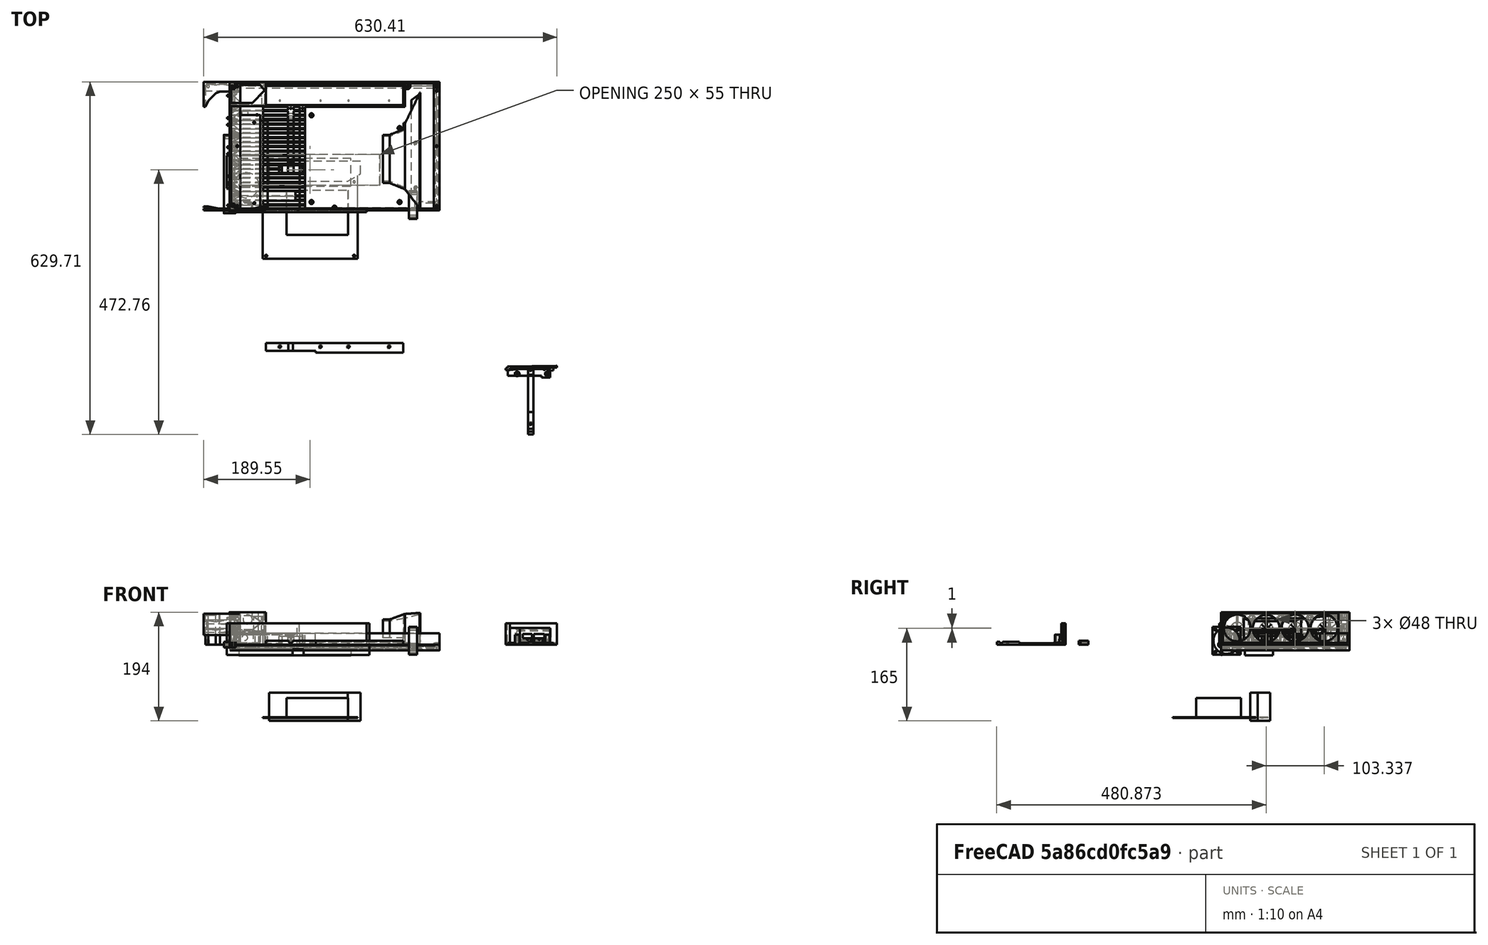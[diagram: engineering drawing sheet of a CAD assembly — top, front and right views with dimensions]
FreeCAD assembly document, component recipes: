
FREECAD ASSEMBLY — COMPONENT RECIPES ("4_fan_duct_version")

This assembly document has 13 components, labeled P0..P12 below (a component is one placed body or linked part). 13 of them carry a construction recipe — the FreeCAD feature program that regenerates the part from scratch, quoted from this document or its linked companion documents; the rest are supplied as boundary geometry only. No exploded tour is included for this assembly.
NOTE — document 2 of 2 of this assembly tour. The two overview renders and the header above are repeated from document 1; the component sections below continue where the previous document stopped.
COMPONENT P2 — recipe-attached ("FAN_SHROUD001", modeled in this document).
Construction recipe (the document's own serialized feature program — sketch geometry with constraints, then the solid features built on it; lengths are millimeters unless a unit is written):

FEATURE [Sketcher::SketchObject] Sketch057
  ArcFitTolerance = 1e-06
  AttachmentSupport = -> [XY_Plane031]
  FullyConstrained = false
  MakeInternals = false
  MapMode = 5
  expr: Constraints[10] = <<components>>.frame_h
  expr: Constraints[21] = <<choices>>.mb_front_edge_gap
  expr: Constraints[25] = 10.16 + 22.86
  expr: Constraints[27] = <<components>>.fan_w + <<choices>>.exit_w + <<choices>>.shroud_mb_space
  expr: Constraints[37] = <<components>>.fan_w
  expr: Constraints[38] = <<components>>.fan_h * 4 + 3 * <<choices>>.fan_gap
  expr: Constraints[40] = <<choices>>.exit_w
  expr: Constraints[71] = <<components>>.fan_h + <<choices>>.fan_gap
  expr: Constraints[9] = <<components>>.frame_w
  sketch-geometry (28):
    g0: LineSegment [constr] StartX=0 StartY=0 StartZ=0 EndX=375 EndY=0 EndZ=0
    g1: LineSegment [constr] StartX=375 StartY=0 StartZ=0 EndX=375 EndY=229.5 EndZ=0
    g2: LineSegment [constr] StartX=375 StartY=229.5 StartZ=0 EndX=0 EndY=229.5 EndZ=0
    g3: LineSegment [constr] StartX=0 StartY=229.5 StartZ=0 EndX=0 EndY=0 EndZ=0
    g4: LineSegment [constr] StartX=140 StartY=180 StartZ=0 EndX=140 EndY=10 EndZ=0
    g5: LineSegment [constr] StartX=140 StartY=10 StartZ=0 EndX=310 EndY=10 EndZ=0
    g6: LineSegment [constr] StartX=310 StartY=10 StartZ=0 EndX=310 EndY=180 EndZ=0
    g7: LineSegment [constr] StartX=310 StartY=180 StartZ=0 EndX=140 EndY=180 EndZ=0
    g8: LineSegment [constr] StartX=303.65 StartY=146.98 StartZ=0 EndX=303.65 EndY=10 EndZ=0
    g9: Circle CenterX=303.65 CenterY=146.98 CenterZ=0 NormalX=0 NormalY=0 NormalZ=1 AngleXU=0 Radius=1.75
    g10: LineSegment [constr] StartX=339 StartY=4 StartZ=0 EndX=356 EndY=4 EndZ=0
    g11: LineSegment [constr] StartX=356 StartY=4 StartZ=0 EndX=356 EndY=210 EndZ=0
    g12: LineSegment [constr] StartX=356 StartY=210 StartZ=0 EndX=339 EndY=210 EndZ=0
    g13: LineSegment [constr] StartX=339 StartY=210 StartZ=0 EndX=339 EndY=4 EndZ=0
    g14: LineSegment [constr] StartX=183 StartY=132 StartZ=0 EndX=183 EndY=52 EndZ=0
    g15: LineSegment [constr] StartX=183 StartY=52 StartZ=0 EndX=293 EndY=52 EndZ=0
    g16: LineSegment [constr] StartX=293 StartY=52 StartZ=0 EndX=293 EndY=132 EndZ=0
    g17: LineSegment [constr] StartX=293 StartY=132 StartZ=0 EndX=183 EndY=132 EndZ=0
    g18: LineSegment StartX=273.053 StartY=132 StartZ=0 EndX=286 EndY=132 EndZ=0
    g19: LineSegment StartX=286 StartY=132 StartZ=0 EndX=309.823 EndY=145.872 EndZ=0
    g20: LineSegment StartX=309.823 StartY=145.872 StartZ=0 EndX=339 EndY=158 EndZ=0
    g21: LineSegment StartX=339 StartY=158 StartZ=0 EndX=356 EndY=158 EndZ=0
    g22: LineSegment StartX=356 StartY=158 StartZ=0 EndX=356 EndY=4 EndZ=0
    g23: LineSegment StartX=356 StartY=4 StartZ=0 EndX=339 EndY=4 EndZ=0
    g24: LineSegment StartX=339 StartY=4 StartZ=0 EndX=309.823 EndY=36.5092 EndZ=0
    g25: LineSegment StartX=309.823 StartY=36.5092 StartZ=0 EndX=286 EndY=52 EndZ=0
    g26: LineSegment StartX=286 StartY=52 StartZ=0 EndX=273.053 EndY=52 EndZ=0
    g27: LineSegment StartX=273.053 StartY=52 StartZ=0 EndX=273.053 EndY=132 EndZ=0
  constraints (76):
    c: Coincident(g0,g1)
    c: Coincident(g1,g2)
    c: Coincident(g2,g3)
    c: Coincident(g3,g0)
    c: Horizontal(g0)
    c: Horizontal(g2)
    c: Vertical(g1)
    c: Vertical(g3)
    c: Coincident(g0,g-1)
    c: DistanceX(g2,g2) = 375
    c: DistanceY(g1,g1) = 229.5
    c: Coincident(g4,g5)
    c: Coincident(g5,g6)
    c: Coincident(g6,g7)
    c: Coincident(g7,g4)
    c: Vertical(g4)
    c: Vertical(g6)
    c: Horizontal(g5)
    c: Horizontal(g7)
    c: Distance(g4,g6) = 170
    c: Distance(g5,g7) = 170
    c: DistanceY(g5) = 10
    c: Vertical(g8)
    c: PointOnObject(g8,g5)
    c: Distance(g8,g6) = 6.35
    c: Distance(g8,g7) = 33.02
    c: Diameter(g9) = 3.5
    c: Distance(g5,g1) = 65
    c: Coincident(g9,g8)
    c: Coincident(g10,g11)
    c: Coincident(g11,g12)
    c: Coincident(g12,g13)
    c: Coincident(g13,g10)
    c: Horizontal(g10)
    c: Horizontal(g12)
    c: Vertical(g11)
    c: Vertical(g13)
    c: DistanceX(g12,g12) = 17
    c: DistanceY(g13,g13) = 206
    c: DistanceY(g10) = 4
    c: Distance(g10,g1) = 19
    c: Coincident(g14,g15)
    c: Coincident(g15,g16)
    c: Coincident(g16,g17)
    c: Coincident(g17,g14)
    c: Vertical(g14)
    c: Vertical(g16)
    c: Horizontal(g15)
    c: Horizontal(g17)
    c: Distance(g14,g16) = 110
    c: Distance(g15,g17) = 80
    c: Distance(g15,g6) = 17
    c: Distance(g15,g5) = 42
    c: Horizontal(g18)
    c: Coincident(g18,g19)
    c: Coincident(g19,g20)
    c: PointOnObject(g20,g13)
    c: Coincident(g20,g21)
    c: PointOnObject(g21,g11)
    c: Horizontal(g21)
    c: Coincident(g21,g22)
    c: Coincident(g22,g10)
    c: Coincident(g22,g23)
    c: Coincident(g23,g10)
    c: Coincident(g23,g24)
    c: Coincident(g24,g25)
    c: Coincident(g25,g26)
    c: Horizontal(g26)
    c: Coincident(g26,g27)
    c: Coincident(g27,g18)
    c: Vertical(g27)
    c: Distance(g20,g12) = 52
    c: PointOnObject(g25,g15)
    c: PointOnObject(g18,g17)
    c: Equal(g18,g26)
    c: Distance(g18,g6) = 24
FEATURE [PartDesign::Plane] DatumPlane010
  AttachmentOffset = pos=(0,0,340) rot=(0,0,1;0rad)
  AttachmentSupport = -> [YZ_Plane031]
  Length = 262.721
  MapMode = 5
  Placement = pos=(340,0,0) rot=(0.57735,0.57735,0.57735;2.0944rad)
  ResizeMode = 0
  Width = 109.471
  expr: .AttachmentOffset.Base.z = <<components>>.frame_w - <<choices>>.exit_w - <<components>>.fan_w + 1
FEATURE [PartDesign::Plane] DatumPlane011
  AttachmentOffset = pos=(0,0,313) rot=(0,0,1;0rad)
  AttachmentSupport = -> [YZ_Plane031]
  Length = 262.721
  MapMode = 5
  Placement = pos=(313,0,0) rot=(0.57735,0.57735,0.57735;2.0944rad)
  ResizeMode = 0
  Width = 109.471
  expr: .AttachmentOffset.Base.z = <<components>>.frame_w - <<choices>>.exit_w - <<components>>.fan_w - <<choices>>.shroud_mb_space + 3
FEATURE [PartDesign::Plane] DatumPlane012
  AttachmentOffset = pos=(0,0,286) rot=(0,0,1;0rad)
  AttachmentSupport = -> [YZ_Plane031]
  Length = 262.721
  MapMode = 5
  Placement = pos=(286,0,0) rot=(0.57735,0.57735,0.57735;2.0944rad)
  ResizeMode = 0
  Width = 109.471
  expr: .AttachmentOffset.Base.z = <<components>>.frame_w - <<choices>>.exit_w - <<components>>.fan_w - <<choices>>.shroud_mb_space - 24
FEATURE [PartDesign::Plane] DatumPlane013
  AttachmentOffset = pos=(0,0,276) rot=(0,0,1;0rad)
  AttachmentSupport = -> [YZ_Plane031]
  Length = 262.721
  MapMode = 5
  Placement = pos=(276,0,0) rot=(0.57735,0.57735,0.57735;2.0944rad)
  ResizeMode = 0
  Width = 109.471
  expr: .AttachmentOffset.Base.z = <<components>>.frame_w - <<choices>>.exit_w - <<components>>.fan_w - <<choices>>.shroud_mb_space - 24 - 10
FEATURE [Sketcher::SketchObject] Sketch058
  ArcFitTolerance = 1e-06
  AttachmentSupport = -> [DatumPlane012]
  FullyConstrained = true
  MakeInternals = false
  MapMode = 5
  Placement = pos=(286,0,0) rot=(0.57735,0.57735,0.57735;2.0944rad)
  expr: Constraints[16] = <<choices>>.shroud_wall_thickness
  sketch-geometry (8):
    g0: LineSegment StartX=49 StartY=12 StartZ=0 EndX=49 EndY=45 EndZ=0
    g1: LineSegment StartX=49 StartY=45 StartZ=0 EndX=135 EndY=45 EndZ=0
    g2: LineSegment StartX=135 StartY=45 StartZ=0 EndX=135 EndY=19 EndZ=0
    g3: LineSegment StartX=135 StartY=19 StartZ=0 EndX=132 EndY=19 EndZ=0
    g4: LineSegment StartX=132 StartY=19 StartZ=0 EndX=132 EndY=42 EndZ=0
    g5: LineSegment StartX=132 StartY=42 StartZ=0 EndX=52 EndY=42 EndZ=0
    g6: LineSegment StartX=52 StartY=42 StartZ=0 EndX=52 EndY=12 EndZ=0
    g7: LineSegment StartX=52 StartY=12 StartZ=0 EndX=49 EndY=12 EndZ=0
  constraints (24):
    c: Vertical(g0)
    c: Coincident(g0,g1)
    c: Horizontal(g1)
    c: Coincident(g1,g2)
    c: Vertical(g2)
    c: Coincident(g2,g3)
    c: Horizontal(g3)
    c: Coincident(g3,g4)
    c: Vertical(g4)
    c: Coincident(g4,g5)
    c: Horizontal(g5)
    c: Coincident(g5,g6)
    c: Vertical(g6)
    c: Coincident(g6,g7)
    c: Coincident(g7,g0)
    c: Horizontal(g7)
    c: DistanceX(g3,g3) = 3
    c: Equal(g7,g3)
    c: DistanceY(g5) = 42
    c: DistanceY(g6,g6) = 30
    c: DistanceY(g4,g4) = 23
    c: DistanceX(g5) = 52
    c: DistanceX(g5,g5) = 80
    c: Distance(g5,g1) = 3
FEATURE [Sketcher::SketchObject] Sketch059
  ArcFitTolerance = 1e-06
  AttachmentSupport = -> [DatumPlane012]
  FullyConstrained = true
  MakeInternals = false
  MapMode = 5
  Placement = pos=(286,0,0) rot=(0.57735,0.57735,0.57735;2.0944rad)
  expr: Constraints[16] = <<choices>>.shroud_wall_thickness
  sketch-geometry (8):
    g0: LineSegment StartX=49 StartY=12 StartZ=0 EndX=49 EndY=45 EndZ=0
    g1: LineSegment StartX=49 StartY=45 StartZ=0 EndX=135 EndY=45 EndZ=0
    g2: LineSegment StartX=135 StartY=45 StartZ=0 EndX=135 EndY=19 EndZ=0
    g3: LineSegment StartX=135 StartY=19 StartZ=0 EndX=132 EndY=19 EndZ=0
    g4: LineSegment StartX=132 StartY=19 StartZ=0 EndX=132 EndY=42 EndZ=0
    g5: LineSegment StartX=132 StartY=42 StartZ=0 EndX=52 EndY=42 EndZ=0
    g6: LineSegment StartX=52 StartY=42 StartZ=0 EndX=52 EndY=12 EndZ=0
    g7: LineSegment StartX=52 StartY=12 StartZ=0 EndX=49 EndY=12 EndZ=0
  constraints (24):
    c: Vertical(g0)
    c: Coincident(g0,g1)
    c: Horizontal(g1)
    c: Coincident(g1,g2)
    c: Vertical(g2)
    c: Coincident(g2,g3)
    c: Horizontal(g3)
    c: Coincident(g3,g4)
    c: Vertical(g4)
    c: Coincident(g4,g5)
    c: Horizontal(g5)
    c: Coincident(g5,g6)
    c: Vertical(g6)
    c: Coincident(g6,g7)
    c: Coincident(g7,g0)
    c: Horizontal(g7)
    c: DistanceX(g3,g3) = 3
    c: Equal(g7,g3)
    c: DistanceY(g5) = 42
    c: DistanceY(g6,g6) = 30
    c: DistanceY(g4,g4) = 23
    c: DistanceX(g5) = 52
    c: DistanceX(g5,g5) = 80
    c: Distance(g0,g5) = 3
FEATURE [PartDesign::Pad] Pad027
  Direction = (1,0,0)
  Length = 12
  Length2 = 10
  Placement = pos=(286,0,0) rot=(0.57735,0.57735,0.57735;2.0944rad)
  Profile = -> Sketch058
  ReferenceAxis = -> Sketch058 [N_Axis]
  Refine = true
  Reversed = true
  Suppressed = false
  Type = 0
FEATURE [Sketcher::SketchObject] Sketch060
  ArcFitTolerance = 1e-06
  AttachmentSupport = -> [DatumPlane011]
  FullyConstrained = false
  MakeInternals = false
  MapMode = 5
  Placement = pos=(313,0,0) rot=(0.57735,0.57735,0.57735;2.0944rad)
  expr: Constraints[17] = <<choices>>.shroud_wall_thickness
  expr: Constraints[25] = <<choices>>.exit_height + 3 - <<choices>>.base_under_mb_thickness - 2
  sketch-geometry (9):
    g0: LineSegment StartX=41 StartY=12 StartZ=0 EndX=41 EndY=47 EndZ=0
    g1: LineSegment StartX=41 StartY=47 StartZ=0 EndX=143 EndY=47 EndZ=0
    g2: LineSegment StartX=143 StartY=47 StartZ=0 EndX=143 EndY=19 EndZ=0
    g3: LineSegment StartX=143 StartY=19 StartZ=0 EndX=146 EndY=19 EndZ=0
    g4: LineSegment StartX=146 StartY=19 StartZ=0 EndX=146 EndY=54.75 EndZ=0
    g5: LineSegment StartX=146 StartY=54.75 StartZ=0 EndX=38 EndY=54.75 EndZ=0
    g6: LineSegment StartX=38 StartY=54.75 StartZ=0 EndX=38 EndY=12 EndZ=0
    g7: LineSegment StartX=38 StartY=12 StartZ=0 EndX=41 EndY=12 EndZ=0
    g8: LineSegment [constr] StartX=0 StartY=42 StartZ=0 EndX=33 EndY=42 EndZ=0
  constraints (27):
    c: Vertical(g0)
    c: Coincident(g0,g1)
    c: Horizontal(g1)
    c: Coincident(g1,g2)
    c: Vertical(g2)
    c: Coincident(g2,g3)
    c: Horizontal(g3)
    c: Coincident(g3,g4)
    c: Vertical(g4)
    c: Coincident(g4,g5)
    c: Horizontal(g5)
    c: Coincident(g5,g6)
    c: Vertical(g6)
    c: Coincident(g6,g7)
    c: Coincident(g7,g0)
    c: Horizontal(g7)
    c: Equal(g7,g3)
    c: DistanceX(g3,g3) = 3
    c: PointOnObject(g8,g-2)
    c: Horizontal(g8)
    c: DistanceY(g8) = 42
    c: Distance(g6,g8) = 30
    c: Distance(g2,g8) = 23
    c: DistanceX(g0) = 41
    c: DistanceX(g2) = 143
    c: DistanceY(g5) = 54.75
    c: Distance(g0,g8) = 5
FEATURE [Sketcher::SketchObject] Sketch061
  ArcFitTolerance = 1e-06
  AttachmentSupport = -> [DatumPlane011]
  FullyConstrained = false
  MakeInternals = false
  MapMode = 5
  Placement = pos=(313,0,0) rot=(0.57735,0.57735,0.57735;2.0944rad)
  expr: Constraints[13] = <<choices>>.shroud_wall_thickness
  expr: Constraints[19] = <<choices>>.exit_height + 3 - <<choices>>.base_under_mb_thickness - 2
  sketch-geometry (20):
    g0: LineSegment StartX=41 StartY=0 StartZ=0 EndX=41 EndY=45.7422 EndZ=0
    g1: LineSegment StartX=42.2578 StartY=47 StartZ=0 EndX=141.742 EndY=47 EndZ=0
    g2: LineSegment [constr] StartX=143 StartY=45.7422 StartZ=0 EndX=143 EndY=0 EndZ=0
    g3: LineSegment [constr] StartX=143 StartY=0 StartZ=0 EndX=146 EndY=0 EndZ=0
    g4: LineSegment [constr] StartX=146 StartY=0 StartZ=0 EndX=146 EndY=53.4922 EndZ=0
    g5: LineSegment StartX=144.742 StartY=54.75 StartZ=0 EndX=39.2578 EndY=54.75 EndZ=0
    g6: LineSegment StartX=38 StartY=53.4922 StartZ=0 EndX=38 EndY=0 EndZ=0
    g7: LineSegment StartX=38 StartY=0 StartZ=0 EndX=41 EndY=0 EndZ=0
    g8: LineSegment [constr] StartX=0 StartY=42 StartZ=0 EndX=33 EndY=42 EndZ=0
    g9: ArcOfCircle CenterX=39.2578 CenterY=53.4922 CenterZ=0 NormalX=0 NormalY=0 NormalZ=1 AngleXU=0 Radius=1.25784 StartAngle=1.5708 EndAngle=3.14159
    g10: GeomPoint [constr] X=38 Y=54.75 Z=0
    g11: ArcOfCircle [constr] CenterX=144.742 CenterY=53.4922 CenterZ=0 NormalX=0 NormalY=0 NormalZ=1 AngleXU=0 Radius=1.25784 StartAngle=-9e-16 EndAngle=1.5708
    g12: GeomPoint [constr] X=146 Y=54.75 Z=0
    g13: ArcOfCircle [constr] CenterX=141.742 CenterY=45.7422 CenterZ=0 NormalX=0 NormalY=0 NormalZ=1 AngleXU=0 Radius=1.25784 StartAngle=-1.8e-15 EndAngle=1.5708
    g14: GeomPoint [constr] X=143 Y=47 Z=0
    g15: ArcOfCircle CenterX=42.2578 CenterY=45.7422 CenterZ=0 NormalX=0 NormalY=0 NormalZ=1 AngleXU=0 Radius=1.25784 StartAngle=1.5708 EndAngle=3.14159
    g16: GeomPoint [constr] X=41 Y=47 Z=0
    g17: LineSegment StartX=141.742 StartY=47 StartZ=0 EndX=154.715 EndY=47 EndZ=0
    g18: LineSegment StartX=154.715 StartY=47 StartZ=0 EndX=154.715 EndY=54.75 EndZ=0
    g19: LineSegment StartX=154.715 StartY=54.75 StartZ=0 EndX=144.742 EndY=54.75 EndZ=0
  constraints (49):
    c: Vertical(g0)
    c: Horizontal(g1)
    c: Vertical(g2)
    c: Coincident(g2,g3)
    c: Horizontal(g3)
    c: Coincident(g3,g4)
    c: Vertical(g4)
    c: Horizontal(g5)
    c: Vertical(g6)
    c: Coincident(g6,g7)
    c: Coincident(g7,g0)
    c: Horizontal(g7)
    c: Equal(g7,g3)
    c: DistanceX(g3,g3) = 3
    c: PointOnObject(g8,g-2)
    c: Horizontal(g8)
    c: DistanceY(g8) = 42
    c: DistanceX(g0) = 41
    c: DistanceX(g2) = 143
    c: DistanceY(g10) = 54.75
    c: PointOnObject(g3,g-1)
    c: PointOnObject(g0,g-1)
    c: PointOnObject(g10,g5)
    c: PointOnObject(g10,g6)
    c: Tangent(g5,g9) = -1.5708
    c: Tangent(g6,g9) = -1.5708
    c: PointOnObject(g12,g4)
    c: PointOnObject(g12,g5)
    c: Tangent(g4,g11) = -1.5708
    c: Tangent(g5,g11) = -1.5708
    c: PointOnObject(g14,g1)
    c: PointOnObject(g14,g2)
    c: Tangent(g1,g13) = 1.5708
    c: Tangent(g2,g13) = 1.5708
    c: PointOnObject(g16,g0)
    c: PointOnObject(g16,g1)
    c: Tangent(g0,g15) = 1.5708
    c: Tangent(g1,g15) = 1.5708
    c: Equal(g15,g9)
    c: Equal(g9,g11)
    c: Equal(g11,g13)
    c: Distance(g1,g8) = 5
    c: Coincident(g1,g17)
    c: Horizontal(g17)
    c: Coincident(g17,g18)
    c: Vertical(g18)
    c: Coincident(g18,g19)
    c: Coincident(g19,g5)
    c: Horizontal(g19)
FEATURE [PartDesign::AdditiveLoft] AdditiveLoft001
  BaseFeature = -> Pad027
  Closed = false
  Placement = pos=(286,0,0) rot=(0.57735,0.57735,0.57735;2.0944rad)
  Profile = -> Sketch060
  Refine = true
  Ruled = false
  Sections = -> [Sketch059]
  Suppressed = false
FEATURE [Sketcher::SketchObject] Sketch062
  ArcFitTolerance = 1e-06
  AttachmentSupport = -> [DatumPlane010]
  FullyConstrained = true
  MakeInternals = false
  MapMode = 5
  Placement = pos=(340,0,0) rot=(0.57735,0.57735,0.57735;2.0944rad)
  expr: Constraints[14] = <<choices>>.exit_height + 3 - <<choices>>.base_under_mb_thickness
  expr: Constraints[17] = <<components>>.fan_h + 4
  sketch-geometry (19):
    g0: LineSegment StartX=3.2 StartY=0 StartZ=0 EndX=3.2 EndY=33.75 EndZ=0
    g1: LineSegment StartX=26.2 StartY=56.75 StartZ=0 EndX=187 EndY=56.75 EndZ=0
    g2: LineSegment [constr] StartX=210 StartY=33.75 StartZ=0 EndX=210 EndY=0 EndZ=0
    g3: LineSegment [constr] StartX=210 StartY=0 StartZ=0 EndX=208 EndY=0 EndZ=0
    g4: LineSegment [constr] StartX=208 StartY=0 StartZ=0 EndX=208 EndY=29 EndZ=0
    g5: LineSegment StartX=183 StartY=54 StartZ=0 EndX=30 EndY=54 EndZ=0
    g6: LineSegment StartX=5 StartY=29 StartZ=0 EndX=5 EndY=0 EndZ=0
    g7: LineSegment StartX=5 StartY=0 StartZ=0 EndX=3.2 EndY=0 EndZ=0
    g8: ArcOfCircle CenterX=30 CenterY=29 CenterZ=0 NormalX=0 NormalY=0 NormalZ=1 AngleXU=0 Radius=25 StartAngle=1.5708 EndAngle=3.14159
    g9: GeomPoint [constr] X=5 Y=54 Z=0
    g10: ArcOfCircle [constr] CenterX=183 CenterY=29 CenterZ=0 NormalX=0 NormalY=0 NormalZ=1 AngleXU=0 Radius=25 StartAngle=0 EndAngle=1.5708
    g11: GeomPoint [constr] X=208 Y=54 Z=0
    g12: ArcOfCircle CenterX=26.2 CenterY=33.75 CenterZ=0 NormalX=0 NormalY=0 NormalZ=1 AngleXU=0 Radius=23 StartAngle=1.5708 EndAngle=3.14159
    g13: GeomPoint [constr] X=3.2 Y=56.75 Z=0
    g14: ArcOfCircle [constr] CenterX=187 CenterY=33.75 CenterZ=0 NormalX=0 NormalY=0 NormalZ=1 AngleXU=0 Radius=23 StartAngle=0 EndAngle=1.5708
    g15: GeomPoint [constr] X=210 Y=56.75 Z=0
    g16: LineSegment StartX=183 StartY=54 StartZ=0 EndX=210 EndY=54 EndZ=0
    g17: LineSegment StartX=210 StartY=54 StartZ=0 EndX=210 EndY=56.75 EndZ=0
    g18: LineSegment StartX=210 StartY=56.75 StartZ=0 EndX=187 EndY=56.75 EndZ=0
  constraints (48):
    c: PointOnObject(g0,g-1)
    c: Vertical(g0)
    c: Horizontal(g1)
    c: PointOnObject(g2,g-1)
    c: Vertical(g2)
    c: Coincident(g2,g3)
    c: PointOnObject(g3,g-1)
    c: Coincident(g3,g4)
    c: Vertical(g4)
    c: Horizontal(g5)
    c: PointOnObject(g6,g-1)
    c: Vertical(g6)
    c: Coincident(g6,g7)
    c: Coincident(g7,g0)
    c: DistanceY(g13) = 56.75
    c: DistanceX(g0) = 3.2
    c: DistanceX(g6) = 5
    c: DistanceY(g9) = 54
    c: DistanceX(g3) = 208
    c: PointOnObject(g9,g5)
    c: PointOnObject(g9,g6)
    c: Tangent(g5,g8) = -1.5708
    c: Tangent(g6,g8) = -1.5708
    c: DistanceX(g3,g3) = 2
    c: PointOnObject(g11,g4)
    c: PointOnObject(g11,g5)
    c: Tangent(g4,g10) = -1.5708
    c: Tangent(g5,g10) = -1.5708
    c: Equal(g8,g10)
    c: PointOnObject(g13,g0)
    c: PointOnObject(g13,g1)
    c: Tangent(g0,g12) = 1.5708
    c: Tangent(g1,g12) = 1.5708
    c: PointOnObject(g15,g1)
    c: PointOnObject(g15,g2)
    c: Tangent(g1,g14) = 1.5708
    c: Tangent(g2,g14) = 1.5708
    c: Equal(g14,g12)
    c: Radius(g12) = 23
    c: Radius(g8) = 25
    c: Coincident(g5,g16)
    c: Horizontal(g16)
    c: Coincident(g16,g17)
    c: Vertical(g17)
    c: Coincident(g17,g18)
    c: Coincident(g18,g1)
    c: Horizontal(g18)
    c: PointOnObject(g16,g2)
FEATURE [PartDesign::AdditiveLoft] AdditiveLoft002
  BaseFeature = -> AdditiveLoft001
  Closed = false
  Placement = pos=(286,0,0) rot=(0.57735,0.57735,0.57735;2.0944rad)
  Profile = -> Sketch062
  Refine = true
  Ruled = false
  Sections = -> [Sketch061]
  Suppressed = false
FEATURE [PartDesign::Plane] DatumPlane014
  AttachmentOffset = pos=(0,0,8) rot=(0,0,1;0rad)
  AttachmentSupport = -> [XY_Plane031]
  Length = 424.115
  MapMode = 5
  Placement = pos=(0,0,8) rot=(0,0,1;0rad)
  ResizeMode = 0
  Width = 293.615
FEATURE [Sketcher::SketchObject] Sketch063
  ArcFitTolerance = 1e-06
  AttachmentSupport = -> [DatumPlane014]
  FullyConstrained = false
  MakeInternals = false
  MapMode = 5
  Placement = pos=(0,0,8) rot=(0,0,1;0rad)
  expr: Constraints[0] = <<components>>.m3_hole
  expr: Constraints[6] = 2 + <<components>>.m3_hole / 2
  sketch-geometry (5):
    g0: Circle CenterX=303.65 CenterY=146.98 CenterZ=0 NormalX=0 NormalY=0 NormalZ=1 AngleXU=0 Radius=1.75
    g1: ArcOfCircle CenterX=303.65 CenterY=146.98 CenterZ=0 NormalX=0 NormalY=0 NormalZ=1 AngleXU=0 Radius=3.75 StartAngle=1.38735 EndAngle=4.15092
    g2: LineSegment StartX=304.334 StartY=150.667 StartZ=0 EndX=319.712 EndY=147.814 EndZ=0
    g3: LineSegment StartX=301.653 StartY=143.806 StartZ=0 EndX=305.391 EndY=141.455 EndZ=0
    g4: LineSegment StartX=305.391 StartY=141.455 StartZ=0 EndX=319.712 EndY=147.814 EndZ=0
  constraints (9):
    c: Diameter(g0) = 3.5
    c: DistanceX(g0) = 303.65
    c: DistanceY(g0) = 146.98
    c: Tangent(g1,g2) = 1.5708
    c: Tangent(g1,g3) = -1.5708
    c: Coincident(g1,g0)
    c: Radius(g1) = 3.75
    c: Coincident(g4,g2)
    c: Coincident(g3,g4)
FEATURE [Sketcher::SketchObject] Sketch076
  ArcFitTolerance = 1e-06
  AttachmentSupport = -> [XY_Plane031]
  FullyConstrained = false
  MakeInternals = false
  MapMode = 5
  expr: Constraints[16] = <<choices>>.shroud_base_screw_x
  expr: Constraints[17] = <<choices>>.shroud_base_screw_y1
  expr: Constraints[18] = <<choices>>.shroud_base_screw_y2
  expr: Constraints[9] = <<components>>.m3_hole
  sketch-geometry (8):
    g0: LineSegment StartX=340 StartY=208 StartZ=0 EndX=340 EndY=3.76862 EndZ=0
    g1: LineSegment StartX=340 StartY=3.76862 StartZ=0 EndX=325 EndY=20.5494 EndZ=0
    g2: LineSegment StartX=325 StartY=20.5494 StartZ=0 EndX=325 EndY=196.984 EndZ=0
    g3: LineSegment StartX=325 StartY=196.984 StartZ=0 EndX=340 EndY=208 EndZ=0
    g4: Circle CenterX=332.5 CenterY=40 CenterZ=0 NormalX=0 NormalY=0 NormalZ=1 AngleXU=0 Radius=1.75
    g5: Circle CenterX=332.5 CenterY=120 CenterZ=0 NormalX=0 NormalY=0 NormalZ=1 AngleXU=0 Radius=1.75
    g6: LineSegment [constr] StartX=332.5 StartY=120 StartZ=0 EndX=332.5 EndY=40 EndZ=0
    g7: LineSegment [constr] StartX=332.5 StartY=40 StartZ=0 EndX=332.5 EndY=0 EndZ=0
  constraints (20):
    c: Vertical(g0)
    c: Coincident(g0,g1)
    c: Coincident(g1,g2)
    c: Vertical(g2)
    c: Coincident(g2,g3)
    c: Coincident(g3,g0)
    c: DistanceX(g0) = 340
    c: DistanceX(g2) = 325
    c: Equal(g5,g4)
    c: Diameter(g5) = 3.5
    c: Coincident(g6,g5)
    c: Coincident(g6,g4)
    c: Vertical(g6)
    c: Coincident(g7,g4)
    c: PointOnObject(g7,g-1)
    c: Vertical(g7)
    c: DistanceX(g7) = 332.5
    c: DistanceY(g4) = 40
    c: DistanceY(g5) = 120
    c: DistanceY(g0) = 208
FEATURE [PartDesign::Pad] Pad037
  BaseFeature = -> AdditiveLoft002
  Direction = (0,0,1)
  Length = 2
  Length2 = 10
  Placement = pos=(286,0,0) rot=(0.57735,0.57735,0.57735;2.0944rad)
  Profile = -> Sketch076
  ReferenceAxis = -> Sketch076 [N_Axis]
  Refine = true
  Suppressed = false
  Type = 0
FEATURE [PartDesign::Chamfer] Chamfer008
  Angle = 45
  Base = -> Pad037 [Edge94,Edge93]
  BaseFeature = -> Pad037
  ChamferType = 0
  FlipDirection = false
  Placement = pos=(286,0,0) rot=(0.57735,0.57735,0.57735;2.0944rad)
  Refine = true
  Size = 1.7
  Size2 = 1
  SupportTransform = false
  Suppressed = false
  UseAllEdges = false
FEATURE [Sketcher::SketchObject] Sketch098
  ArcFitTolerance = 1e-06
  AttachmentSupport = -> [DatumPlane010]
  FullyConstrained = false
  MakeInternals = false
  MapMode = 5
  Placement = pos=(340,0,0) rot=(0.57735,0.57735,0.57735;2.0944rad)
  expr: Constraints[14] = <<choices>>.exit_height + 3 - <<choices>>.base_under_mb_thickness
  expr: Constraints[17] = <<components>>.fan_h + 4
  sketch-geometry (24):
    g0: LineSegment StartX=3.2 StartY=0 StartZ=0 EndX=3.2 EndY=33.75 EndZ=0
    g1: LineSegment StartX=26.2 StartY=56.75 StartZ=0 EndX=209.995 EndY=56.75 EndZ=0
    g2: LineSegment StartX=210 StartY=56.745 StartZ=0 EndX=210 EndY=0 EndZ=0
    g3: LineSegment StartX=210 StartY=0 StartZ=0 EndX=208 EndY=0 EndZ=0
    g4: LineSegment [constr] StartX=208 StartY=0 StartZ=0 EndX=208 EndY=30 EndZ=0
    g5: LineSegment [constr] StartX=184 StartY=54 StartZ=0 EndX=29 EndY=54 EndZ=0
    g6: LineSegment [constr] StartX=5 StartY=30 StartZ=0 EndX=5 EndY=0 EndZ=0
    g7: LineSegment StartX=5 StartY=0 StartZ=0 EndX=3.2 EndY=0 EndZ=0
    g8: ArcOfCircle [constr] CenterX=29 CenterY=30 CenterZ=0 NormalX=0 NormalY=0 NormalZ=1 AngleXU=0 Radius=24 StartAngle=1.5708 EndAngle=3.14159
    g9: GeomPoint [constr] X=5 Y=54 Z=0
    g10: ArcOfCircle [constr] CenterX=184 CenterY=30 CenterZ=0 NormalX=0 NormalY=0 NormalZ=1 AngleXU=0 Radius=24 StartAngle=0 EndAngle=1.5708
    g11: GeomPoint [constr] X=208 Y=54 Z=0
    g12: ArcOfCircle CenterX=26.2 CenterY=33.75 CenterZ=0 NormalX=0 NormalY=0 NormalZ=1 AngleXU=0 Radius=23 StartAngle=1.5708 EndAngle=3.14159
    g13: GeomPoint [constr] X=3.2 Y=56.75 Z=0
    g14: ArcOfCircle CenterX=209.995 CenterY=56.745 CenterZ=0 NormalX=0 NormalY=0 NormalZ=1 AngleXU=0 Radius=0.005 StartAngle=-6.315e-13 EndAngle=1.5708
    g15: GeomPoint [constr] X=210 Y=56.75 Z=0
    g16: LineSegment StartX=5 StartY=0 StartZ=0 EndX=208 EndY=0 EndZ=0
    g17: Circle CenterX=29 CenterY=30 CenterZ=0 NormalX=0 NormalY=0 NormalZ=1 AngleXU=0 Radius=24
    g18: Circle CenterX=184 CenterY=30 CenterZ=0 NormalX=0 NormalY=0 NormalZ=1 AngleXU=0 Radius=24
    g19: Circle CenterX=80.6634 CenterY=29 CenterZ=0 NormalX=0 NormalY=0 NormalZ=1 AngleXU=0 Radius=24
    g20: Circle CenterX=132.327 CenterY=30 CenterZ=0 NormalX=0 NormalY=0 NormalZ=1 AngleXU=0 Radius=24
    g21: LineSegment [constr] StartX=29 StartY=30 StartZ=0 EndX=80.6634 EndY=29 EndZ=0
    g22: LineSegment [constr] StartX=80.6634 StartY=29 StartZ=0 EndX=132.327 EndY=30 EndZ=0
    g23: LineSegment [constr] StartX=132.327 StartY=30 StartZ=0 EndX=184 EndY=30 EndZ=0
  constraints (57):
    c: PointOnObject(g0,g-1)
    c: Vertical(g0)
    c: Horizontal(g1)
    c: PointOnObject(g2,g-1)
    c: Vertical(g2)
    c: Coincident(g2,g3)
    c: PointOnObject(g3,g-1)
    c: Coincident(g3,g4)
    c: Vertical(g4)
    c: Horizontal(g5)
    c: PointOnObject(g6,g-1)
    c: Vertical(g6)
    c: Coincident(g6,g7)
    c: Coincident(g7,g0)
    c: DistanceY(g13) = 56.75
    c: DistanceX(g0) = 3.2
    c: DistanceX(g6) = 5
    c: DistanceY(g9) = 54
    c: DistanceX(g3) = 208
    c: PointOnObject(g9,g5)
    c: PointOnObject(g9,g6)
    c: Tangent(g5,g8) = -1.5708
    c: Tangent(g6,g8) = -1.5708
    c: DistanceX(g3,g3) = 2
    c: PointOnObject(g11,g4)
    c: PointOnObject(g11,g5)
    c: Tangent(g4,g10) = -1.5708
    c: Tangent(g5,g10) = -1.5708
    c: Equal(g8,g10)
    c: PointOnObject(g13,g0)
    c: PointOnObject(g13,g1)
    c: Tangent(g0,g12) = 1.5708
    c: Tangent(g1,g12) = 1.5708
    c: PointOnObject(g15,g1)
    c: PointOnObject(g15,g2)
    c: Tangent(g1,g14) = 1.5708
    c: Tangent(g2,g14) = 1.5708
    c: Radius(g12) = 23
    c: Radius(g8) = 24
    c: Coincident(g16,g6)
    c: Coincident(g16,g3)
    c: Coincident(g17,g8)
    c: Coincident(g18,g10)
    c: Equal(g17,g19)
    c: Equal(g19,g20)
    c: Equal(g20,g18)
    c: Equal(g17,g8)
    c: Coincident(g21,g8)
    c: Coincident(g21,g19)
    c: Coincident(g22,g19)
    c: Coincident(g22,g20)
    c: Coincident(g23,g20)
    c: Coincident(g23,g10)
    c: Horizontal(g23)
    c: Equal(g23,g22)
    c: Equal(g22,g21)
    c: Radius(g14) = 0.005
FEATURE [PartDesign::Pad] Pad052
  BaseFeature = -> Chamfer008
  Direction = (1,0,0)
  Length = 1
  Length2 = 10
  Midplane = true
  Placement = pos=(286,0,0) rot=(0.57735,0.57735,0.57735;2.0944rad)
  Profile = -> Sketch098
  ReferenceAxis = -> Sketch098 [N_Axis]
  Refine = true
  Suppressed = false
  Type = 0
FEATURE [Sketcher::SketchObject] Sketch099
  ArcFitTolerance = 1e-06
  AttachmentSupport = -> [DatumPlane011]
  FullyConstrained = false
  MakeInternals = false
  MapMode = 5
  Placement = pos=(313,0,0) rot=(0.57735,0.57735,0.57735;2.0944rad)
  sketch-geometry (4):
    g0: LineSegment StartX=144.683 StartY=54.6555 StartZ=0 EndX=144.683 EndY=13.734 EndZ=0
    g1: LineSegment StartX=144.683 StartY=13.734 StartZ=0 EndX=156.349 EndY=13.734 EndZ=0
    g2: LineSegment StartX=156.349 StartY=13.734 StartZ=0 EndX=156.349 EndY=54.6555 EndZ=0
    g3: LineSegment StartX=156.349 StartY=54.6555 StartZ=0 EndX=144.683 EndY=54.6555 EndZ=0
  constraints (8):
    c: Coincident(g0,g1)
    c: Coincident(g1,g2)
    c: Coincident(g2,g3)
    c: Coincident(g3,g0)
    c: Vertical(g0)
    c: Vertical(g2)
    c: Horizontal(g1)
    c: Horizontal(g3)
FEATURE [PartDesign::Pad] Pad053
  BaseFeature = -> Pad052
  Direction = (1,0,0)
  Length = 2
  Length2 = 10
  Placement = pos=(286,0,0) rot=(0.57735,0.57735,0.57735;2.0944rad)
  Profile = -> Sketch099
  ReferenceAxis = -> Sketch099 [N_Axis]
  Refine = true
  Reversed = true
  Suppressed = false
  Type = 0
FEATURE [PartDesign::Body] Body014
  AllowCompound = false
  Group = -> [Sketch057,DatumPlane010,DatumPlane011,DatumPlane012,DatumPlane013,Pad027,Sketch058,Sketch059,Sketch060,Sketch061,AdditiveLoft001,Sketch062,AdditiveLoft002,DatumPlane014,Sketch063,Sketch076,Pad037,Chamfer008,Sketch098,Pad052,Sketch099,Pad053]
  Origin = -> Origin031
  Tip = -> Pad053
COMPONENT P3 — recipe-attached ("FRAME001", modeled in this document).
Construction recipe (the document's own serialized feature program — sketch geometry with constraints, then the solid features built on it; lengths are millimeters unless a unit is written):

FEATURE [Sketcher::SketchObject] Sketch006
  ArcFitTolerance = 1e-06
  AttachmentSupport = -> [XY_Plane007]
  FullyConstrained = false
  MakeInternals = false
  MapMode = 5
  expr: Constraints[20] = <<components>>.frame_w
  expr: Constraints[21] = <<components>>.frame_h
  expr: Constraints[22] = <<choices>>.corner
  sketch-geometry (12):
    g0: LineSegment StartX=1 StartY=1.7071e-12 StartZ=0 EndX=374 EndY=1.7071e-12 EndZ=0
    g1: LineSegment StartX=375 StartY=1 StartZ=0 EndX=375 EndY=228.5 EndZ=0
    g2: LineSegment StartX=374 StartY=229.5 StartZ=0 EndX=1 EndY=229.5 EndZ=0
    g3: LineSegment StartX=1.7071e-12 StartY=228.5 StartZ=0 EndX=1.7071e-12 EndY=1 EndZ=0
    g4: ArcOfCircle CenterX=1 CenterY=1 CenterZ=0 NormalX=0 NormalY=0 NormalZ=1 AngleXU=0 Radius=1 StartAngle=3.14159 EndAngle=4.71239
    g5: ArcOfCircle CenterX=374 CenterY=1 CenterZ=0 NormalX=0 NormalY=0 NormalZ=1 AngleXU=0 Radius=1 StartAngle=4.71239 EndAngle=6.28319
    g6: ArcOfCircle CenterX=374 CenterY=228.5 CenterZ=0 NormalX=0 NormalY=0 NormalZ=1 AngleXU=0 Radius=1 StartAngle=-2.76916e-11 EndAngle=1.5708
    g7: ArcOfCircle CenterX=1 CenterY=228.5 CenterZ=0 NormalX=0 NormalY=0 NormalZ=1 AngleXU=0 Radius=1 StartAngle=1.5708 EndAngle=3.14159
    g8: GeomPoint [constr] X=0 Y=0 Z=0
    g9: GeomPoint [constr] X=375 Y=229.5 Z=0
    g10: GeomPoint [constr] X=14.2421 Y=11.9526 Z=0
    g11: GeomPoint [constr] X=324.973 Y=165.011 Z=0
  constraints (23):
    c: Tangent(g0,g4) = -1.5708
    c: Tangent(g0,g5) = -1.5708
    c: Tangent(g1,g5) = -1.5708
    c: Tangent(g1,g6) = -1.5708
    c: Tangent(g2,g6) = -1.5708
    c: Tangent(g2,g7) = -1.5708
    c: Tangent(g3,g7) = -1.5708
    c: Tangent(g3,g4) = -1.5708
    c: Horizontal(g0)
    c: Horizontal(g2)
    c: Vertical(g1)
    c: Vertical(g3)
    c: Equal(g4,g5)
    c: Equal(g5,g6)
    c: Equal(g6,g7)
    c: PointOnObject(g8,g0)
    c: PointOnObject(g8,g3)
    c: PointOnObject(g9,g1)
    c: PointOnObject(g9,g2)
    c: Coincident(g8,g-1)
    c: DistanceX(g9) = 375
    c: DistanceY(g9) = 229.5
    c: Radius(g6) = 1
FEATURE [PartDesign::Pad] Pad006
  Direction = (0,0,1)
  Length = 10
  Length2 = 10
  Profile = -> Sketch006
  ReferenceAxis = -> Sketch006 [N_Axis]
  Refine = true
  Reversed = true
  Suppressed = false
  Type = 0
  expr: Length = <<components>>.frame_d
FEATURE [Sketcher::SketchObject] Sketch007
  ArcFitTolerance = 1e-06
  AttachmentSupport = -> [XY_Plane007]
  FullyConstrained = true
  MakeInternals = false
  MapMode = 5
  expr: Constraints[19] = <<components>>.screen_w + 2 * <<choices>>.margin
  expr: Constraints[20] = <<components>>.screen_h + 2 * <<choices>>.margin
  expr: Constraints[21] = <<components>>.screen_glass_corner_radius
  expr: Constraints[22] = <<choices>>.bezel
  expr: Constraints[23] = <<choices>>.bezel
  sketch-geometry (10):
    g0: LineSegment StartX=4 StartY=3 StartZ=0 EndX=371 EndY=3 EndZ=0
    g1: LineSegment StartX=372 StartY=4 StartZ=0 EndX=372 EndY=225.5 EndZ=0
    g2: LineSegment StartX=371 StartY=226.5 StartZ=0 EndX=4 EndY=226.5 EndZ=0
    g3: LineSegment StartX=3 StartY=225.5 StartZ=0 EndX=3 EndY=4 EndZ=0
    g4: ArcOfCircle CenterX=4 CenterY=4 CenterZ=0 NormalX=0 NormalY=0 NormalZ=1 AngleXU=0 Radius=1 StartAngle=3.14159 EndAngle=4.71239
    g5: ArcOfCircle CenterX=371 CenterY=4 CenterZ=0 NormalX=0 NormalY=0 NormalZ=1 AngleXU=0 Radius=1 StartAngle=4.71239 EndAngle=6.28319
    g6: ArcOfCircle CenterX=371 CenterY=225.5 CenterZ=0 NormalX=0 NormalY=0 NormalZ=1 AngleXU=0 Radius=1 StartAngle=-1.15e-14 EndAngle=1.5708
    g7: ArcOfCircle CenterX=4 CenterY=225.5 CenterZ=0 NormalX=0 NormalY=0 NormalZ=1 AngleXU=0 Radius=1 StartAngle=1.5708 EndAngle=3.14159
    g8: GeomPoint [constr] X=3 Y=3 Z=0
    g9: GeomPoint [constr] X=372 Y=226.5 Z=0
  constraints (24):
    c: Tangent(g0,g4) = -1.5708
    c: Tangent(g0,g5) = -1.5708
    c: Tangent(g1,g5) = -1.5708
    c: Tangent(g1,g6) = -1.5708
    c: Tangent(g2,g6) = -1.5708
    c: Tangent(g2,g7) = -1.5708
    c: Tangent(g3,g7) = -1.5708
    c: Tangent(g3,g4) = -1.5708
    c: Horizontal(g0)
    c: Horizontal(g2)
    c: Vertical(g1)
    c: Vertical(g3)
    c: Equal(g4,g5)
    c: Equal(g5,g6)
    c: Equal(g6,g7)
    c: PointOnObject(g8,g0)
    c: PointOnObject(g8,g3)
    c: PointOnObject(g9,g1)
    c: PointOnObject(g9,g2)
    c: Distance(g1,g3) = 369
    c: Distance(g2,g0) = 223.5
    c: Radius(g4) = 1
    c: DistanceY(g8) = 3
    c: DistanceX(g8) = 3
FEATURE [PartDesign::Pocket] Pocket
  BaseFeature = -> Pad006
  Direction = (0,0,-1)
  Length = 3
  Length2 = 5
  Profile = -> Sketch007
  ReferenceAxis = -> Sketch007 [N_Axis]
  Refine = true
  Suppressed = false
  Type = 0
  expr: Length = <<choices>>.frame_protective_height + <<components>>.screen_glass_d
FEATURE [Sketcher::SketchObject] Sketch008
  ArcFitTolerance = 1e-06
  AttachmentSupport = -> [XY_Plane007]
  FullyConstrained = true
  MakeInternals = false
  MapMode = 5
  expr: Constraints[10] = <<choices>>.bezel + <<choices>>.margin + 11
  expr: Constraints[11] = <<components>>.frame_h - <<choices>>.bezel - <<choices>>.margin - 3.5
  expr: Constraints[12] = <<choices>>.bezel + <<choices>>.margin + 6
  expr: Constraints[13] = <<components>>.frame_w - <<choices>>.bezel - <<choices>>.margin - 2
  expr: Constraints[9] = <<choices>>.bezel + <<choices>>.margin + 0.8
  sketch-geometry (24):
    g0: LineSegment StartX=10.05 StartY=222.45 StartZ=0 EndX=368.95 EndY=222.45 EndZ=0
    g1: LineSegment StartX=369.45 StartY=221.95 StartZ=0 EndX=369.45 EndY=15.55 EndZ=0
    g2: LineSegment StartX=368.95 StartY=15.05 StartZ=0 EndX=339.95 EndY=15.05 EndZ=0
    g3: LineSegment StartX=339.45 StartY=14.55 StartZ=0 EndX=339.45 EndY=4.85 EndZ=0
    g4: LineSegment StartX=338.95 StartY=4.35 StartZ=0 EndX=40.05 EndY=4.35 EndZ=0
    g5: LineSegment StartX=39.55 StartY=4.85 StartZ=0 EndX=39.55 EndY=14.05 EndZ=0
    g6: LineSegment StartX=39.05 StartY=14.55 StartZ=0 EndX=10.05 EndY=14.55 EndZ=0
    g7: LineSegment StartX=9.55 StartY=15.05 StartZ=0 EndX=9.55 EndY=221.95 EndZ=0
    g8: ArcOfCircle CenterX=10.05 CenterY=221.95 CenterZ=0 NormalX=0 NormalY=0 NormalZ=1 AngleXU=0 Radius=0.5 StartAngle=1.5708 EndAngle=3.14159
    g9: GeomPoint [constr] X=9.55 Y=222.45 Z=0
    g10: ArcOfCircle CenterX=368.95 CenterY=221.95 CenterZ=0 NormalX=0 NormalY=0 NormalZ=1 AngleXU=0 Radius=0.5 StartAngle=-1.87e-14 EndAngle=1.5708
    g11: GeomPoint [constr] X=369.45 Y=222.45 Z=0
    g12: ArcOfCircle CenterX=368.95 CenterY=15.55 CenterZ=0 NormalX=0 NormalY=0 NormalZ=1 AngleXU=0 Radius=0.5 StartAngle=4.71239 EndAngle=6.28319
    g13: GeomPoint [constr] X=369.45 Y=15.05 Z=0
    g14: ArcOfCircle CenterX=339.95 CenterY=14.55 CenterZ=0 NormalX=0 NormalY=0 NormalZ=1 AngleXU=0 Radius=0.5 StartAngle=1.5708 EndAngle=3.14159
    g15: GeomPoint [constr] X=339.45 Y=15.05 Z=0
    g16: ArcOfCircle CenterX=338.95 CenterY=4.85 CenterZ=0 NormalX=0 NormalY=0 NormalZ=1 AngleXU=0 Radius=0.5 StartAngle=4.71239 EndAngle=6.28319
    g17: GeomPoint [constr] X=339.45 Y=4.35 Z=0
    g18: ArcOfCircle CenterX=40.05 CenterY=4.85 CenterZ=0 NormalX=0 NormalY=0 NormalZ=1 AngleXU=0 Radius=0.5 StartAngle=3.14159 EndAngle=4.71239
    g19: GeomPoint [constr] X=39.55 Y=4.35 Z=0
    g20: ArcOfCircle CenterX=39.05 CenterY=14.05 CenterZ=0 NormalX=0 NormalY=0 NormalZ=1 AngleXU=0 Radius=0.5 StartAngle=5e-16 EndAngle=1.5708
    g21: GeomPoint [constr] X=39.55 Y=14.55 Z=0
    g22: ArcOfCircle CenterX=10.05 CenterY=15.05 CenterZ=0 NormalX=0 NormalY=0 NormalZ=1 AngleXU=0 Radius=0.5 StartAngle=3.14159 EndAngle=4.71239
    g23: GeomPoint [constr] X=9.55 Y=14.55 Z=0
  constraints (56):
    c: Horizontal(g0)
    c: Vertical(g1)
    c: Horizontal(g2)
    c: Vertical(g3)
    c: Horizontal(g4)
    c: Vertical(g5)
    c: Horizontal(g6)
    c: Vertical(g7)
    c: DistanceX(g23,g21) = 30
    c: DistanceY(g19) = 4.35
    c: DistanceY(g21) = 14.55
    c: DistanceY(g9) = 222.45
    c: DistanceX(g9) = 9.55
    c: DistanceX(g11) = 369.45
    c: PointOnObject(g9,g7)
    c: PointOnObject(g9,g0)
    c: Tangent(g7,g8) = 1.5708
    c: Tangent(g0,g8) = 1.5708
    c: PointOnObject(g11,g0)
    c: PointOnObject(g11,g1)
    c: Tangent(g0,g10) = 1.5708
    c: Tangent(g1,g10) = 1.5708
    c: PointOnObject(g13,g2)
    c: PointOnObject(g13,g1)
    c: Tangent(g2,g12) = 1.5708
    c: Tangent(g1,g12) = 1.5708
    c: PointOnObject(g15,g2)
    c: PointOnObject(g15,g3)
    c: Tangent(g2,g14) = -1.5708
    c: Tangent(g3,g14) = -1.5708
    c: PointOnObject(g17,g3)
    c: PointOnObject(g17,g4)
    c: Tangent(g3,g16) = 1.5708
    c: Tangent(g4,g16) = 1.5708
    c: PointOnObject(g19,g4)
    c: PointOnObject(g19,g5)
    c: Tangent(g4,g18) = 1.5708
    c: Tangent(g5,g18) = 1.5708
    c: PointOnObject(g21,g5)
    c: PointOnObject(g21,g6)
    c: Tangent(g5,g20) = -1.5708
    c: Tangent(g6,g20) = -1.5708
    c: PointOnObject(g23,g6)
    c: PointOnObject(g23,g7)
    c: Tangent(g6,g22) = 1.5708
    c: Tangent(g7,g22) = 1.5708
    c: Equal(g22,g8)
    c: Radius(g8) = 0.5
    c: Equal(g20,g18)
    c: Equal(g18,g22)
    c: Equal(g16,g14)
    c: Equal(g14,g12)
    c: Equal(g12,g10)
    c: Equal(g10,g8)
    c: PointOnObject(g14,g6)
    c: Equal(g2,g6)
FEATURE [PartDesign::Pocket] Pocket001
  BaseFeature = -> Pocket
  Direction = (0,0,-1)
  Length = 8.75
  Length2 = 5
  Profile = -> Sketch008
  ReferenceAxis = -> Sketch008 [N_Axis]
  Refine = true
  Suppressed = false
  Type = 0
  expr: Length = <<components>>.screen_panel_d + <<choices>>.frame_protective_height + <<choices>>.screen_panel_foam_thickness
FEATURE [Sketcher::SketchObject] Sketch009
  ArcFitTolerance = 1e-06
  AttachmentSupport = -> [XY_Plane007]
  FullyConstrained = true
  MakeInternals = false
  MapMode = 5
  expr: Constraints[22] = <<choices>>.bezel + <<choices>>.margin + 41.5
  expr: Constraints[23] = <<choices>>.bezel + <<choices>>.margin + 15
  sketch-geometry (10):
    g0: LineSegment StartX=19.55 StartY=45.05 StartZ=0 EndX=267.55 EndY=45.05 EndZ=0
    g1: LineSegment StartX=268.55 StartY=46.05 StartZ=0 EndX=268.55 EndY=99.05 EndZ=0
    g2: LineSegment StartX=267.55 StartY=100.05 StartZ=0 EndX=19.55 EndY=100.05 EndZ=0
    g3: LineSegment StartX=18.55 StartY=99.05 StartZ=0 EndX=18.55 EndY=46.05 EndZ=0
    g4: ArcOfCircle CenterX=19.55 CenterY=46.05 CenterZ=0 NormalX=0 NormalY=0 NormalZ=1 AngleXU=0 Radius=1 StartAngle=3.14159 EndAngle=4.71239
    g5: ArcOfCircle CenterX=267.55 CenterY=46.05 CenterZ=0 NormalX=0 NormalY=0 NormalZ=1 AngleXU=0 Radius=1 StartAngle=4.71239 EndAngle=6.28319
    g6: ArcOfCircle CenterX=267.55 CenterY=99.05 CenterZ=0 NormalX=0 NormalY=0 NormalZ=1 AngleXU=0 Radius=1 StartAngle=8e-16 EndAngle=1.5708
    g7: ArcOfCircle CenterX=19.55 CenterY=99.05 CenterZ=0 NormalX=0 NormalY=0 NormalZ=1 AngleXU=0 Radius=1 StartAngle=1.5708 EndAngle=3.14159
    g8: GeomPoint [constr] X=18.55 Y=45.05 Z=0
    g9: GeomPoint [constr] X=268.55 Y=100.05 Z=0
  constraints (24):
    c: Tangent(g0,g4) = -1.5708
    c: Tangent(g0,g5) = -1.5708
    c: Tangent(g1,g5) = -1.5708
    c: Tangent(g1,g6) = -1.5708
    c: Tangent(g2,g6) = -1.5708
    c: Tangent(g2,g7) = -1.5708
    c: Tangent(g3,g7) = -1.5708
    c: Tangent(g3,g4) = -1.5708
    c: Horizontal(g0)
    c: Horizontal(g2)
    c: Vertical(g1)
    c: Vertical(g3)
    c: Equal(g4,g5)
    c: Equal(g5,g6)
    c: Equal(g6,g7)
    c: PointOnObject(g8,g0)
    c: PointOnObject(g8,g3)
    c: PointOnObject(g9,g1)
    c: PointOnObject(g9,g2)
    c: Distance(g1,g3) = 250
    c: Distance(g0,g2) = 55
    c: Radius(g5) = 1
    c: DistanceY(g0) = 45.05
    c: DistanceX(g8) = 18.55
FEATURE [PartDesign::Pocket] Pocket002
  BaseFeature = -> Pocket001
  Direction = (0,0,-1)
  Length = 0
  Length2 = 5
  Profile = -> Sketch009
  ReferenceAxis = -> Sketch009 [N_Axis]
  Refine = true
  Suppressed = false
  Type = 1
FEATURE [PartDesign::Plane] DatumPlane016
  AttachmentOffset = pos=(0,0,-10) rot=(0,0,1;0rad)
  AttachmentSupport = -> [XY_Plane007]
  Length = 463.812
  MapMode = 5
  Placement = pos=(0,0,-10) rot=(0,0,1;0rad)
  ResizeMode = 0
  Width = 318.312
FEATURE [Sketcher::SketchObject] Sketch071
  ArcFitTolerance = 1e-06
  AttachmentSupport = -> [DatumPlane016]
  FullyConstrained = true
  MakeInternals = false
  MapMode = 5
  Placement = pos=(0,0,-10) rot=(0,0,1;0rad)
  expr: Constraints[10] = <<components>>.frame_h
  expr: Constraints[30] = <<components>>.m3_threadhole
  expr: Constraints[43] = 188 + 8
  expr: Constraints[54] = <<components>>.m3_threadhole
  expr: Constraints[9] = <<components>>.frame_w
  sketch-geometry (22):
    g0: LineSegment [constr] StartX=0 StartY=0 StartZ=0 EndX=375 EndY=0 EndZ=0
    g1: LineSegment [constr] StartX=375 StartY=0 StartZ=0 EndX=375 EndY=229.5 EndZ=0
    g2: LineSegment [constr] StartX=375 StartY=229.5 StartZ=0 EndX=0 EndY=229.5 EndZ=0
    g3: LineSegment [constr] StartX=0 StartY=229.5 StartZ=0 EndX=0 EndY=0 EndZ=0
    g4: LineSegment [constr] StartX=5 StartY=8 StartZ=0 EndX=370 EndY=8 EndZ=0
    g5: LineSegment [constr] StartX=370 StartY=8 StartZ=0 EndX=370 EndY=221.5 EndZ=0
    g6: LineSegment [constr] StartX=370 StartY=221.5 StartZ=0 EndX=5 EndY=221.5 EndZ=0
    g7: LineSegment [constr] StartX=5 StartY=221.5 StartZ=0 EndX=5 EndY=8 EndZ=0
    g8: Circle CenterX=5 CenterY=221.5 CenterZ=0 NormalX=0 NormalY=0 NormalZ=1 AngleXU=0 Radius=1.25
    g9: Circle CenterX=5 CenterY=8 CenterZ=0 NormalX=0 NormalY=0 NormalZ=1 AngleXU=0 Radius=1.25
    g10: Circle CenterX=370 CenterY=8 CenterZ=0 NormalX=0 NormalY=0 NormalZ=1 AngleXU=0 Radius=1.25
    g11: Circle CenterX=370 CenterY=221.5 CenterZ=0 NormalX=0 NormalY=0 NormalZ=1 AngleXU=0 Radius=1.25
    g12: Circle CenterX=370 CenterY=114.75 CenterZ=0 NormalX=0 NormalY=0 NormalZ=1 AngleXU=0 Radius=1.25
    g13: LineSegment [constr] StartX=5 StartY=196 StartZ=0 EndX=370 EndY=196 EndZ=0
    g14: GeomPoint [constr] X=187.5 Y=196 Z=0
    g15: LineSegment [constr] StartX=162.5 StartY=196 StartZ=0 EndX=212.5 EndY=196 EndZ=0
    g16: Circle CenterX=162.5 CenterY=196 CenterZ=0 NormalX=0 NormalY=0 NormalZ=1 AngleXU=0 Radius=1.25
    g17: Circle CenterX=212.5 CenterY=196 CenterZ=0 NormalX=0 NormalY=0 NormalZ=1 AngleXU=0 Radius=1.25
    g18: Circle CenterX=90 CenterY=196 CenterZ=0 NormalX=0 NormalY=0 NormalZ=1 AngleXU=0 Radius=1.25
    g19: Circle CenterX=285 CenterY=196 CenterZ=0 NormalX=0 NormalY=0 NormalZ=1 AngleXU=0 Radius=1.25
    g20: Circle CenterX=187.5 CenterY=5 CenterZ=0 NormalX=0 NormalY=0 NormalZ=1 AngleXU=0 Radius=1.25
    g21: LineSegment [constr] StartX=187.5 StartY=0 StartZ=0 EndX=187.5 EndY=5 EndZ=0
  constraints (55):
    c: Coincident(g0,g1)
    c: Coincident(g1,g2)
    c: Coincident(g2,g3)
    c: Coincident(g3,g0)
    c: Horizontal(g0)
    c: Horizontal(g2)
    c: Vertical(g1)
    c: Vertical(g3)
    c: Coincident(g0,g-1)
    c: DistanceX(g2,g2) = 375
    c: DistanceY(g1,g1) = 229.5
    c: Coincident(g4,g5)
    c: Coincident(g5,g6)
    c: Coincident(g6,g7)
    c: Coincident(g7,g4)
    c: Horizontal(g4)
    c: Horizontal(g6)
    c: Vertical(g5)
    c: Vertical(g7)
    c: DistanceX(g4) = 5
    c: DistanceY(g4) = 8
    c: Distance(g6,g2) = 8
    c: Distance(g5,g1) = 5
    c: Coincident(g8,g6)
    c: Coincident(g9,g4)
    c: Coincident(g10,g4)
    c: Coincident(g11,g5)
    c: Equal(g11,g8)
    c: Equal(g8,g9)
    c: Equal(g9,g10)
    c: Diameter(g10) = 2.5
    c: Symmetric(g5,g5,g12)
    c: Equal(g12,g10)
    c: PointOnObject(g13,g7)
    c: PointOnObject(g13,g5)
    c: Horizontal(g13)
    c: Symmetric(g13,g13,g14)
    c: PointOnObject(g15,g13)
    c: Symmetric(g15,g15,g14)
    c: Coincident(g16,g15)
    c: Coincident(g17,g15)
    c: Equal(g17,g16)
    c: Equal(g16,g8)
    c: DistanceY(g14) = 196
    c: DistanceX(g15,g15) = 50
    c: PointOnObject(g18,g13)
    c: Equal(g19,g18)
    c: Equal(g18,g17)
    c: Symmetric(g18,g19,g14)
    c: DistanceX(g18) = 90
    c: Symmetric(g0,g0,g21)
    c: Coincident(g21,g20)
    c: Vertical(g21)
    c: DistanceY(g21,g21) = 5
    c: Diameter(g20) = 2.5
FEATURE [PartDesign::Pocket] Pocket032
  BaseFeature = -> Pocket002
  Direction = (0,0,-1)
  Length = 5
  Length2 = 5
  Profile = -> Sketch071
  ReferenceAxis = -> Sketch071 [N_Axis]
  Refine = true
  Reversed = true
  Suppressed = false
  Type = 0
FEATURE [PartDesign::Body] Body003
  AllowCompound = false
  Group = -> [Sketch006,Pad006,Sketch007,Pocket,Sketch008,Pocket001,Sketch009,Pocket002,DatumPlane016,Sketch071,Pocket032]
  Origin = -> Origin007
  Tip = -> Pocket032
COMPONENT P4 — recipe-attached ("FRONT_VENT001", modeled in this document).
Construction recipe (the document's own serialized feature program — sketch geometry with constraints, then the solid features built on it; lengths are millimeters unless a unit is written):

FEATURE [Sketcher::SketchObject] Sketch074
  ArcFitTolerance = 1e-06
  AttachmentSupport = -> [XZ_Plane037]
  FullyConstrained = true
  MakeInternals = false
  MapMode = 5
  Placement = pos=(0,0,0) rot=(1,0,0;1.5708rad)
  expr: Constraints[10] = <<choices>>.exit_height + 3 - <<choices>>.base_max_thickness
  expr: Constraints[9] = <<components>>.frame_w - 2 * 65
  sketch-geometry (4):
    g0: LineSegment StartX=0 StartY=0 StartZ=0 EndX=245 EndY=0 EndZ=0
    g1: LineSegment StartX=245 StartY=0 StartZ=0 EndX=245 EndY=38 EndZ=0
    g2: LineSegment StartX=245 StartY=38 StartZ=0 EndX=0 EndY=38 EndZ=0
    g3: LineSegment StartX=0 StartY=38 StartZ=0 EndX=0 EndY=0 EndZ=0
  constraints (11):
    c: Coincident(g0,g1)
    c: Coincident(g1,g2)
    c: Coincident(g2,g3)
    c: Coincident(g3,g0)
    c: Horizontal(g0)
    c: Horizontal(g2)
    c: Vertical(g1)
    c: Vertical(g3)
    c: Coincident(g0,g-1)
    c: DistanceX(g2,g2) = 245
    c: DistanceY(g1,g1) = 38
FEATURE [PartDesign::Pad] Pad035
  Direction = (0,-1,2e-16)
  Length = 3
  Length2 = 10
  Placement = pos=(0,0,0) rot=(1,0,0;1.5708rad)
  Profile = -> Sketch074
  ReferenceAxis = -> Sketch074 [N_Axis]
  Refine = true
  Suppressed = false
  Type = 0
FEATURE [Sketcher::SketchObject] Sketch075
  ArcFitTolerance = 1e-06
  AttachmentSupport = -> [XZ_Plane037]
  FullyConstrained = false
  MakeInternals = false
  MapMode = 5
  Placement = pos=(0,0,0) rot=(1,0,0;1.5708rad)
  expr: Constraints[10] = 5 + <<components>>.frame_w - 2 * 65
  expr: Constraints[7] = <<choices>>.exit_height + 3 - <<choices>>.base_max_thickness
  expr: Constraints[9] = -<<choices>>.base_max_thickness + <<choices>>.base_under_mb_thickness + 0.5
  sketch-geometry (14):
    g0: LineSegment StartX=-5 StartY=38 StartZ=0 EndX=-5 EndY=-18.25 EndZ=0
    g1: LineSegment StartX=250 StartY=-18.25 StartZ=0 EndX=250 EndY=38 EndZ=0
    g2: LineSegment StartX=250 StartY=38 StartZ=0 EndX=-5 EndY=38 EndZ=0
    g3: LineSegment [constr] StartX=112.5 StartY=-28.25 StartZ=0 EndX=132.5 EndY=-28.25 EndZ=0
    g4: LineSegment StartX=132.5 StartY=-8.25 StartZ=0 EndX=112.5 EndY=-8.25 EndZ=0
    g5: GeomPoint [constr] X=122.5 Y=-18.25 Z=0
    g6: LineSegment StartX=112.5 StartY=-8.25 StartZ=0 EndX=112.5 EndY=-18.25 EndZ=0
    g7: LineSegment [constr] StartX=112.5 StartY=-18.25 StartZ=0 EndX=112.5 EndY=-28.25 EndZ=0
    g8: LineSegment [constr] StartX=132.5 StartY=-28.25 StartZ=0 EndX=132.5 EndY=-18.25 EndZ=0
    g9: LineSegment StartX=132.5 StartY=-18.25 StartZ=0 EndX=132.5 EndY=-8.25 EndZ=0
    g10: LineSegment [constr] StartX=122.5 StartY=-18.25 StartZ=0 EndX=132.5 EndY=-18.25 EndZ=0
    g11: LineSegment StartX=132.5 StartY=-18.25 StartZ=0 EndX=250 EndY=-18.25 EndZ=0
    g12: LineSegment StartX=-5 StartY=-18.25 StartZ=0 EndX=112.5 EndY=-18.25 EndZ=0
    g13: LineSegment [constr] StartX=112.5 StartY=-18.25 StartZ=0 EndX=122.5 EndY=-18.25 EndZ=0
  constraints (36):
    c: Coincident(g0,g12)
    c: Coincident(g11,g1)
    c: Coincident(g1,g2)
    c: Coincident(g2,g0)
    c: Vertical(g0)
    c: Vertical(g1)
    c: Horizontal(g2)
    c: DistanceY(g0) = 38
    c: DistanceX(g0) = -5
    c: DistanceY(g0) = -18.25
    c: DistanceX(g1) = 250
    c: Coincident(g3,g8)
    c: Coincident(g9,g4)
    c: Coincident(g4,g6)
    c: Coincident(g7,g3)
    c: Horizontal(g3)
    c: Horizontal(g4)
    c: Symmetric(g4,g3,g5)
    c: Distance(g8,g7) = 20
    c: Distance(g3,g4) = 20
    c: Symmetric(g12,g11,g5)
    c: Coincident(g6,g7)
    c: Vertical(g6)
    c: Vertical(g7)
    c: Coincident(g8,g9)
    c: Vertical(g8)
    c: Vertical(g9)
    c: Coincident(g13,g10)
    c: Coincident(g10,g11)
    c: Horizontal(g10)
    c: Horizontal(g11)
    c: Coincident(g8,g10)
    c: Coincident(g12,g13)
    c: Horizontal(g12)
    c: Horizontal(g13)
    c: Coincident(g12,g6)
FEATURE [PartDesign::Pad] Pad036
  BaseFeature = -> Pad035
  Direction = (0,-1,2e-16)
  Length = 2
  Length2 = 10
  Placement = pos=(0,0,0) rot=(1,0,0;1.5708rad)
  Profile = -> Sketch075
  ReferenceAxis = -> Sketch075 [N_Axis]
  Refine = true
  Reversed = true
  Suppressed = false
  Type = 0
FEATURE [Sketcher::SketchObject] Sketch087
  ArcFitTolerance = 1e-06
  AttachmentSupport = -> [XY_Plane037]
  FullyConstrained = true
  MakeInternals = false
  MapMode = 5
  expr: Constraints[2] = 245 / 2
  sketch-geometry (1):
    g0: Circle CenterX=122.5 CenterY=2 CenterZ=0 NormalX=0 NormalY=0 NormalZ=1 AngleXU=0 Radius=1.75
  constraints (3):
    c: Diameter(g0) = 3.5
    c: DistanceY(g0) = 2
    c: DistanceX(g0) = 122.5
FEATURE [PartDesign::Pocket] Pocket037
  BaseFeature = -> Pad036
  Direction = (0,0,-1)
  Length = 5
  Length2 = 5
  Midplane = true
  Placement = pos=(0,0,0) rot=(1,0,0;1.5708rad)
  Profile = -> Sketch087
  ReferenceAxis = -> Sketch087 [N_Axis]
  Refine = true
  Suppressed = false
  Type = 1
FEATURE [PartDesign::Body] Body017
  AllowCompound = false
  Group = -> [Sketch074,Pad035,Sketch075,Pad036,Sketch087,Pocket037]
  Origin = -> Origin037
  Tip = -> Pocket037
COMPONENT P5 — recipe-attached ("GPU001", modeled in this document).
Construction recipe (the document's own serialized feature program — sketch geometry with constraints, then the solid features built on it; lengths are millimeters unless a unit is written):

FEATURE [Sketcher::SketchObject] Sketch011
  ArcFitTolerance = 1e-06
  AttachmentSupport = -> [XY_Plane009]
  FullyConstrained = true
  MakeInternals = false
  MapMode = 5
  expr: Constraints[10] = <<components>>.gpu_w
  expr: Constraints[9] = <<components>>.gpu_h
  sketch-geometry (5):
    g0: LineSegment StartX=0 StartY=0 StartZ=0 EndX=68 EndY=0 EndZ=0
    g1: LineSegment StartX=68 StartY=0 StartZ=0 EndX=68 EndY=160 EndZ=0
    g2: LineSegment StartX=68 StartY=160 StartZ=0 EndX=0 EndY=160 EndZ=0
    g3: LineSegment StartX=0 StartY=160 StartZ=0 EndX=0 EndY=0 EndZ=0
    g4: Circle CenterX=30 CenterY=45 CenterZ=0 NormalX=0 NormalY=0 NormalZ=1 AngleXU=0 Radius=22.5
  constraints (14):
    c: Coincident(g0,g1)
    c: Coincident(g1,g2)
    c: Coincident(g2,g3)
    c: Coincident(g3,g0)
    c: Horizontal(g0)
    c: Horizontal(g2)
    c: Vertical(g1)
    c: Vertical(g3)
    c: Coincident(g0,g-1)
    c: DistanceY(g1,g1) = 160
    c: DistanceX(g2,g2) = 68
    c: Diameter(g4) = 45
    c: DistanceX(g4) = 30
    c: DistanceY(g4) = 45
FEATURE [PartDesign::Pad] Pad009
  Direction = (0,0,1)
  Length = 20
  Length2 = 10
  Profile = -> Sketch011
  ReferenceAxis = -> Sketch011 [N_Axis]
  Refine = true
  Suppressed = false
  Type = 0
  expr: Length = <<components>>.gpu_d
FEATURE [PartDesign::Plane] DatumPlane019
  AttachmentOffset = pos=(0,0,-160) rot=(0,0,1;0rad)
  AttachmentSupport = -> [XZ_Plane009]
  Length = 106.638
  MapMode = 5
  Placement = pos=(0,160,-3.55e-14) rot=(1,0,0;1.5708rad)
  ResizeMode = 0
  Width = 63.6382
  expr: .AttachmentOffset.Base.z = -<<components>>.gpu_h
FEATURE [Sketcher::SketchObject] Sketch077  label="this will be the end sockets sketch"
  ArcFitTolerance = 1e-06
  AttachmentSupport = -> [DatumPlane019]
  FullyConstrained = false
  MakeInternals = false
  MapMode = 5
  Placement = pos=(0,160,-3.55e-14) rot=(1,0,0;1.5708rad)
  expr: Constraints[18] = <<components>>.m3_hole
  sketch-geometry (11):
    g0: LineSegment StartX=22.9359 StartY=12.1138 StartZ=0 EndX=39.5359 EndY=12.1138 EndZ=0
    g1: LineSegment StartX=39.5359 StartY=12.1138 StartZ=0 EndX=39.5359 EndY=6.11381 EndZ=0
    g2: LineSegment StartX=39.5359 StartY=6.11381 StartZ=0 EndX=36.2624 EndY=5.21381 EndZ=0
    g3: LineSegment StartX=36.2624 StartY=5.21381 StartZ=0 EndX=26.2095 EndY=5.21381 EndZ=0
    g4: LineSegment StartX=26.2095 StartY=5.21381 StartZ=0 EndX=22.9359 EndY=6.11381 EndZ=0
    g5: LineSegment StartX=22.9359 StartY=6.11381 StartZ=0 EndX=22.9359 EndY=12.1138 EndZ=0
    g6: LineSegment [constr] StartX=31.2359 StartY=12.1138 StartZ=0 EndX=31.2359 EndY=14.49 EndZ=0
    g7: Circle CenterX=31.2359 CenterY=14.49 CenterZ=0 NormalX=0 NormalY=0 NormalZ=1 AngleXU=0 Radius=1.75
    g8: LineSegment [constr] StartX=31.2359 StartY=14.49 StartZ=0 EndX=52.2359 EndY=14.49 EndZ=0
    g9: Circle CenterX=52.2359 CenterY=14.49 CenterZ=0 NormalX=0 NormalY=0 NormalZ=1 AngleXU=0 Radius=1.75
    g10: LineSegment [constr] StartX=52.2359 StartY=14.49 StartZ=0 EndX=66.2359 EndY=14.49 EndZ=0
  constraints (27):
    c: Horizontal(g0)
    c: Coincident(g0,g1)
    c: Vertical(g1)
    c: Coincident(g1,g2)
    c: Coincident(g2,g3)
    c: Coincident(g3,g4)
    c: Coincident(g4,g5)
    c: Coincident(g5,g0)
    c: Vertical(g5)
    c: Horizontal(g3)
    c: Distance(g3,g0) = 6.9
    c: DistanceX(g0,g0) = 16.6
    c: DistanceY(g1,g1) = 6
    c: Equal(g5,g1)
    c: Equal(g4,g2)
    c: Symmetric(g0,g0,g6)
    c: Vertical(g6)
    c: Coincident(g7,g6)
    c: Diameter(g7) = 3.5
    c: Distance(g8) = 21
    c: Coincident(g8,g6)
    c: Horizontal(g8)
    c: Coincident(g9,g8)
    c: Equal(g9,g7)
    c: Coincident(g10,g8)
    c: Horizontal(g10)
    c: DistanceX(g10,g10) = 14
FEATURE [PartDesign::Body] Body004
  AllowCompound = false
  Group = -> [Sketch011,Pad009,DatumPlane019,Sketch077]
  Origin = -> Origin009
  Tip = -> Pad009
COMPONENT P6 — recipe-attached ("GPU_bracket001", modeled in this document).
Construction recipe (the document's own serialized feature program — sketch geometry with constraints, then the solid features built on it; lengths are millimeters unless a unit is written):

FEATURE [Sketcher::SketchObject] Sketch079
  ArcFitTolerance = 1e-06
  AttachmentSupport = -> [XY_Plane039]
  FullyConstrained = false
  MakeInternals = false
  MapMode = 5
  expr: Constraints[18] = <<components>>.m3_insert_r
  sketch-geometry (26):
    g0: LineSegment StartX=496.422 StartY=-278.414 StartZ=0 EndX=496.557 EndY=-289.648 EndZ=0
    g1: LineSegment StartX=577.825 StartY=-280.368 StartZ=0 EndX=584.414 EndY=-280.288 EndZ=0
    g2: LineSegment StartX=584.414 StartY=-280.288 StartZ=0 EndX=584.391 EndY=-278.351 EndZ=0
    g3: LineSegment StartX=583.379 StartY=-277.363 StartZ=0 EndX=496.422 EndY=-278.414 EndZ=0
    g4: ArcOfCircle CenterX=583.391 CenterY=-278.363 CenterZ=0 NormalX=0 NormalY=0 NormalZ=1 AngleXU=0 Radius=1 StartAngle=0.012082 EndAngle=1.58288
    g5: GeomPoint [constr] X=584.378 Y=-277.351 Z=0
    g6: Circle CenterX=561.991 CenterY=-283.107 CenterZ=0 NormalX=0 NormalY=0 NormalZ=1 AngleXU=0 Radius=1.75
    g7: Circle CenterX=540.95 CenterY=-283.354 CenterZ=0 NormalX=0 NormalY=0 NormalZ=1 AngleXU=0 Radius=1.75
    g8: LineSegment [constr] StartX=567.426 StartY=-288.792 StartZ=0 EndX=567.462 EndY=-291.792 EndZ=0
    g9: Circle CenterX=567.462 CenterY=-291.792 CenterZ=0 NormalX=0 NormalY=0 NormalZ=1 AngleXU=0 Radius=2.25
    g10: LineSegment [constr] StartX=567.426 StartY=-288.792 StartZ=0 EndX=567.39 EndY=-285.805 EndZ=0
    g11: LineSegment [constr] StartX=567.39 StartY=-285.805 StartZ=0 EndX=567.366 EndY=-283.805 EndZ=0
    g12: LineSegment [constr] StartX=567.39 StartY=-285.805 StartZ=0 EndX=571.544 EndY=-285.755 EndZ=0
    g13: LineSegment [constr] StartX=577.925 StartY=-288.665 StartZ=0 EndX=577.885 EndY=-285.369 EndZ=0
    g14: LineSegment StartX=577.885 StartY=-285.369 StartZ=0 EndX=577.825 EndY=-280.368 EndZ=0
    g15: LineSegment [constr] StartX=572.498 StartY=-288.731 StartZ=0 EndX=577.925 EndY=-288.665 EndZ=0
    g16: LineSegment StartX=577.885 StartY=-285.369 StartZ=0 EndX=572.498 EndY=-286.538 EndZ=0
    g17: LineSegment StartX=572.498 StartY=-286.538 StartZ=0 EndX=572.498 EndY=-288.731 EndZ=0
    g18: LineSegment StartX=572.498 StartY=-288.731 StartZ=0 EndX=572.615 EndY=-298.391 EndZ=0
    g19: LineSegment StartX=572.615 StartY=-298.391 StartZ=0 EndX=557.218 EndY=-298.577 EndZ=0
    g20: LineSegment [constr] StartX=496.557 StartY=-289.648 StartZ=0 EndX=557.102 EndY=-288.917 EndZ=0
    g21: LineSegment [constr] StartX=557.102 StartY=-288.917 StartZ=0 EndX=572.498 EndY=-288.731 EndZ=0
    g22: LineSegment StartX=496.557 StartY=-289.648 StartZ=0 EndX=496.557 EndY=-295.02 EndZ=0
    g23: LineSegment StartX=496.557 StartY=-295.02 StartZ=0 EndX=557.175 EndY=-295.02 EndZ=0
    g24: LineSegment StartX=557.218 StartY=-298.577 StartZ=0 EndX=557.175 EndY=-295.02 EndZ=0
    g25: LineSegment [constr] StartX=557.175 StartY=-295.02 StartZ=0 EndX=557.102 EndY=-288.917 EndZ=0
  constraints (61):
    c: Coincident(g0,g20)
    c: Coincident(g15,g13)
    c: Coincident(g14,g1)
    c: Coincident(g1,g2)
    c: Coincident(g3,g0)
    c: Perpendicular(g3,g0)
    c: PointOnObject(g5,g2)
    c: PointOnObject(g5,g3)
    c: Tangent(g2,g4) = -1.5708
    c: Tangent(g3,g4) = -1.5708
    c: Radius(g4) = 1
    c: Perpendicular(g1,g2)
    c: Perpendicular(g2,g3)
    c: Diameter(g6) = 3.5
    c: Diameter(g7) = 3.5
    c: DistanceX(g15) = 577.925
    c: DistanceY(g15) = -288.665
    c: Coincident(g9,g8)
    c: Diameter(g9) = 4.5
    c: Coincident(g10,g8)
    c: Coincident(g10,g11)
    c: Parallel(g10,g8)
    c: Parallel(g11,g8)
    c: Coincident(g12,g10)
    c: Perpendicular(g10,g12)
    c: Distance(g11) = 2
    c: Distance(g8) = 3
    c: Coincident(g13,g14)
    c: Perpendicular(g13,g1)
    c: Perpendicular(g14,g1)
    c: Distance(g8,g13) = 10.5
    c: Coincident(g21,g15)
    c: Perpendicular(g0,g15)
    c: Coincident(g13,g16)
    c: Coincident(g16,g17)
    c: Coincident(g17,g21)
    c: Vertical(g17)
    c: Coincident(g17,g18)
    c: Coincident(g18,g19)
    c: Coincident(g19,g24)
    c: Coincident(g20,g21)
    c: Perpendicular(g0,g20)
    c: Perpendicular(g0,g21)
    c: PointOnObject(g8,g20)
    c: Perpendicular(g20,g8)
    c: Coincident(g20,g25)
    c: DistanceX(g0) = 496.422
    c: DistanceY(g0) = -278.414
    c: Perpendicular(g18,g15)
    c: Perpendicular(g18,g19)
    c: Coincident(g0,g22)
    c: Vertical(g22)
    c: Coincident(g22,g23)
    c: Horizontal(g23)
    c: Coincident(g24,g25)
    c: Perpendicular(g24,g20)
    c: Perpendicular(g25,g20)
    c: Coincident(g24,g23)
    c: DistanceX(g0) = 496.557
    c: DistanceX(g19) = 557.218
    c: DistanceY(g19) = -298.577
FEATURE [PartDesign::Pad] Pad039
  Direction = (0,0,1)
  Length = 3
  Length2 = 10
  Profile = -> Sketch079
  ReferenceAxis = -> Sketch079 [N_Axis]
  Refine = true
  Suppressed = false
  Type = 0
FEATURE [Sketcher::SketchObject] Sketch080
  ArcFitTolerance = 1e-06
  AttachmentSupport = -> [XY_Plane039]
  FullyConstrained = false
  MakeInternals = false
  MapMode = 5
  expr: Constraints[1] = <<components>>.m3_insert_r
  expr: Constraints[2] = <<components>>.m3_insert_r + 4
  sketch-geometry (5):
    g0: Circle CenterX=567.5 CenterY=-291.8 CenterZ=0 NormalX=0 NormalY=0 NormalZ=1 AngleXU=0 Radius=2.25
    g1: Circle CenterX=567.5 CenterY=-291.8 CenterZ=0 NormalX=0 NormalY=0 NormalZ=1 AngleXU=0 Radius=4.25
    g2: Circle CenterX=513.5 CenterY=-291.8 CenterZ=0 NormalX=0 NormalY=0 NormalZ=1 AngleXU=0 Radius=2.25
    g3: Circle CenterX=513.5 CenterY=-291.8 CenterZ=0 NormalX=0 NormalY=0 NormalZ=1 AngleXU=0 Radius=4.25
    g4: LineSegment [constr] StartX=567.5 StartY=-291.8 StartZ=0 EndX=486.353 EndY=-291.8 EndZ=0
  constraints (12):
    c: Coincident(g1,g0)
    c: Diameter(g0) = 4.5
    c: Diameter(g1) = 8.5
    c: DistanceX(g0) = 567.5
    c: DistanceY(g0) = -291.8
    c: Coincident(g3,g2)
    c: Equal(g2,g0)
    c: Equal(g3,g1)
    c: Distance(g0,g2) = 54
    c: Coincident(g4,g0)
    c: Horizontal(g4)
    c: PointOnObject(g2,g4)
FEATURE [PartDesign::Pad] Pad040
  BaseFeature = -> Pad039
  Direction = (0,0,1)
  Length = 18
  Length2 = 10
  Profile = -> Sketch080
  ReferenceAxis = -> Sketch080 [N_Axis]
  Refine = true
  Suppressed = false
  Type = 0
FEATURE [Sketcher::SketchObject] Sketch081
  ArcFitTolerance = 1e-06
  AttachmentSupport = -> [XY_Plane039]
  FullyConstrained = false
  MakeInternals = false
  MapMode = 5
  sketch-geometry (15):
    g0: LineSegment StartX=584.414 StartY=-280.301 StartZ=0 EndX=584.394 EndY=-278.452 EndZ=0
    g1: LineSegment StartX=583.383 StartY=-277.463 StartZ=0 EndX=496.422 EndY=-278.414 EndZ=0
    g2: ArcOfCircle CenterX=583.394 CenterY=-278.463 CenterZ=0 NormalX=0 NormalY=0 NormalZ=1 AngleXU=0 Radius=1 StartAngle=0.0109358 EndAngle=1.58173
    g3: GeomPoint [constr] X=584.383 Y=-277.452 Z=0
    g4: LineSegment StartX=496.422 StartY=-278.414 StartZ=0 EndX=496.465 EndY=-281.514 EndZ=0
    g5: LineSegment [constr] StartX=496.465 StartY=-281.514 StartZ=0 EndX=500.406 EndY=-281.46 EndZ=0
    g6: LineSegment StartX=496.465 StartY=-281.514 StartZ=0 EndX=492.964 EndY=-281.563 EndZ=0
    g7: LineSegment StartX=492.964 StartY=-281.563 StartZ=0 EndX=493.008 EndY=-284.801 EndZ=0
    g8: LineSegment StartX=493.008 StartY=-284.801 StartZ=0 EndX=500.451 EndY=-284.698 EndZ=0
    g9: LineSegment StartX=500.451 StartY=-284.698 StartZ=0 EndX=500.406 EndY=-281.46 EndZ=0
    g10: LineSegment StartX=500.406 StartY=-281.46 StartZ=0 EndX=518.146 EndY=-281.215 EndZ=0
    g11: LineSegment StartX=518.146 StartY=-281.215 StartZ=0 EndX=537.146 EndY=-280.953 EndZ=0
    g12: LineSegment StartX=537.146 StartY=-280.953 StartZ=0 EndX=544.404 EndY=-280.853 EndZ=0
    g13: LineSegment StartX=544.404 StartY=-280.853 StartZ=0 EndX=556.056 EndY=-280.692 EndZ=0
    g14: LineSegment StartX=556.056 StartY=-280.692 StartZ=0 EndX=584.414 EndY=-280.301 EndZ=0
  constraints (37):
    c: PointOnObject(g3,g0)
    c: PointOnObject(g3,g1)
    c: Tangent(g0,g2) = -1.5708
    c: Tangent(g1,g2) = -1.5708
    c: Radius(g2) = 1
    c: Perpendicular(g0,g1)
    c: DistanceX(g1) = 496.422
    c: DistanceY(g1) = -278.414
    c: DistanceX(g0) = 584.414
    c: DistanceY(g0) = -280.301
    c: Coincident(g1,g4)
    c: Coincident(g4,g5)
    c: Coincident(g5,g10)
    c: Coincident(g4,g6)
    c: Coincident(g6,g7)
    c: Coincident(g7,g8)
    c: Coincident(g8,g9)
    c: Coincident(g9,g5)
    c: Perpendicular(g8,g9)
    c: Perpendicular(g8,g7)
    c: Perpendicular(g6,g7)
    c: Perpendicular(g4,g6)
    c: DistanceX(g8) = 500.451
    c: DistanceY(g8) = -284.698
    c: Coincident(g14,g0)
    c: Coincident(g10,g11)
    c: Perpendicular(g10,g9)
    c: Parallel(g5,g10)
    c: Coincident(g11,g12)
    c: Perpendicular(g11,g9)
    c: Coincident(g12,g13)
    c: Perpendicular(g12,g9)
    c: Coincident(g13,g14)
    c: Perpendicular(g13,g9)
    c: Perpendicular(g14,g9)
    c: DistanceY(g5) = -281.46
    c: DistanceX(g11,g11) = 19
FEATURE [PartDesign::Pad] Pad041
  BaseFeature = -> Pad040
  Direction = (0,0,1)
  Length = 38
  Length2 = 10
  Profile = -> Sketch081
  ReferenceAxis = -> Sketch081 [N_Axis]
  Refine = true
  Suppressed = false
  Type = 0
  expr: Length = <<choices>>.exit_height + 3 - <<choices>>.base_max_thickness
FEATURE [PartDesign::Plane] DatumPlane020
  AttachmentOffset = pos=(0,0,3) rot=(0,0,1;0rad)
  AttachmentSupport = -> [XY_Plane039]
  Length = 698.227
  MapMode = 5
  Placement = pos=(0,0,3) rot=(0,0,1;0rad)
  ResizeMode = 0
  Width = 412.39
FEATURE [Sketcher::SketchObject] Sketch082
  ArcFitTolerance = 1e-06
  AttachmentSupport = -> [DatumPlane020]
  FullyConstrained = false
  MakeInternals = false
  MapMode = 5
  Placement = pos=(0,0,3) rot=(0,0,1;0rad)
  sketch-geometry (2):
    g0: Circle CenterX=562.014 CenterY=-283.062 CenterZ=0 NormalX=0 NormalY=0 NormalZ=1 AngleXU=0 Radius=3
    g1: Circle CenterX=540.918 CenterY=-283.394 CenterZ=0 NormalX=0 NormalY=0 NormalZ=1 AngleXU=0 Radius=3
  constraints (2):
    c: Diameter(g0) = 6
    c: Equal(g0,g1)
FEATURE [Sketcher::SketchObject] Sketch084
  ArcFitTolerance = 1e-06
  AttachmentSupport = -> [XY_Plane039]
  FullyConstrained = false
  MakeInternals = false
  MapMode = 5
  sketch-geometry (4):
    g0: LineSegment StartX=567.72 StartY=-289.014 StartZ=0 EndX=571.009 EndY=-289.014 EndZ=0
    g1: LineSegment StartX=571.009 StartY=-289.014 StartZ=0 EndX=571.009 EndY=-279.004 EndZ=0
    g2: LineSegment StartX=571.009 StartY=-279.004 StartZ=0 EndX=567.72 EndY=-279.004 EndZ=0
    g3: LineSegment StartX=567.72 StartY=-279.004 StartZ=0 EndX=567.72 EndY=-289.014 EndZ=0
  constraints (8):
    c: Coincident(g0,g1)
    c: Coincident(g1,g2)
    c: Coincident(g2,g3)
    c: Coincident(g3,g0)
    c: Horizontal(g0)
    c: Horizontal(g2)
    c: Vertical(g1)
    c: Vertical(g3)
FEATURE [Sketcher::SketchObject] Sketch093
  ArcFitTolerance = 1e-06
  AttachmentSupport = -> [XY_Plane039]
  FullyConstrained = false
  MakeInternals = false
  MapMode = 5
  sketch-geometry (23):
    g0: LineSegment StartX=584.414 StartY=-280.301 StartZ=0 EndX=584.414 EndY=-279.414 EndZ=0
    g1: LineSegment StartX=583.414 StartY=-278.414 StartZ=0 EndX=496.422 EndY=-278.414 EndZ=0
    g2: ArcOfCircle CenterX=583.414 CenterY=-279.414 CenterZ=0 NormalX=0 NormalY=0 NormalZ=1 AngleXU=0 Radius=1 StartAngle=4.14e-14 EndAngle=1.5708
    g3: GeomPoint [constr] X=584.414 Y=-278.414 Z=0
    g4: LineSegment StartX=496.422 StartY=-278.414 StartZ=0 EndX=496.465 EndY=-281.514 EndZ=0
    g5: LineSegment [constr] StartX=496.465 StartY=-281.514 StartZ=0 EndX=500.406 EndY=-281.46 EndZ=0
    g6: LineSegment StartX=496.465 StartY=-281.514 StartZ=0 EndX=492.964 EndY=-281.563 EndZ=0
    g7: LineSegment StartX=492.964 StartY=-281.563 StartZ=0 EndX=493.008 EndY=-284.801 EndZ=0
    g8: LineSegment StartX=493.008 StartY=-284.801 StartZ=0 EndX=500.451 EndY=-284.698 EndZ=0
    g9: LineSegment [constr] StartX=500.451 StartY=-284.698 StartZ=0 EndX=500.406 EndY=-281.46 EndZ=0
    g10: LineSegment [constr] StartX=500.406 StartY=-281.46 StartZ=0 EndX=518.147 EndY=-281.215 EndZ=0
    g11: LineSegment [constr] StartX=518.147 StartY=-281.215 StartZ=0 EndX=537.147 EndY=-280.953 EndZ=0
    g12: LineSegment [constr] StartX=537.147 StartY=-280.953 StartZ=0 EndX=544.403 EndY=-280.853 EndZ=0
    g13: LineSegment [constr] StartX=544.403 StartY=-280.853 StartZ=0 EndX=572.362 EndY=-280.467 EndZ=0
    g14: LineSegment StartX=572.362 StartY=-280.467 StartZ=0 EndX=584.414 EndY=-280.301 EndZ=0
    g15: LineSegment [constr] StartX=518.147 StartY=-281.215 StartZ=0 EndX=518.147 EndY=-282.853 EndZ=0
    g16: LineSegment StartX=518.147 StartY=-282.853 StartZ=0 EndX=537.147 EndY=-282.853 EndZ=0
    g17: LineSegment [constr] StartX=537.147 StartY=-282.853 StartZ=0 EndX=537.147 EndY=-280.953 EndZ=0
    g18: LineSegment [constr] StartX=544.403 StartY=-280.853 StartZ=0 EndX=544.403 EndY=-282.853 EndZ=0
    g19: LineSegment StartX=544.403 StartY=-282.853 StartZ=0 EndX=572.362 EndY=-282.853 EndZ=0
    g20: LineSegment StartX=572.362 StartY=-282.853 StartZ=0 EndX=572.362 EndY=-280.467 EndZ=0
    g21: LineSegment StartX=500.451 StartY=-284.698 StartZ=0 EndX=518.147 EndY=-282.853 EndZ=0
    g22: LineSegment StartX=537.147 StartY=-282.853 StartZ=0 EndX=544.403 EndY=-282.853 EndZ=0
  constraints (58):
    c: PointOnObject(g3,g0)
    c: PointOnObject(g3,g1)
    c: Tangent(g0,g2) = -1.5708
    c: Tangent(g1,g2) = -1.5708
    c: Radius(g2) = 1
    c: Perpendicular(g0,g1)
    c: DistanceX(g1) = 496.422
    c: DistanceY(g1) = -278.414
    c: DistanceX(g0) = 584.414
    c: DistanceY(g0) = -280.301
    c: Coincident(g1,g4)
    c: Coincident(g4,g5)
    c: Coincident(g5,g10)
    c: Coincident(g4,g6)
    c: Coincident(g6,g7)
    c: Coincident(g7,g8)
    c: Coincident(g8,g9)
    c: Coincident(g9,g5)
    c: Perpendicular(g8,g9)
    c: Perpendicular(g8,g7)
    c: Perpendicular(g6,g7)
    c: Perpendicular(g4,g6)
    c: DistanceX(g8) = 500.451
    c: DistanceY(g8) = -284.698
    c: Coincident(g14,g0)
    c: Coincident(g10,g11)
    c: Perpendicular(g10,g9)
    c: Parallel(g5,g10)
    c: Coincident(g11,g12)
    c: Perpendicular(g11,g9)
    c: Coincident(g12,g13)
    c: Perpendicular(g12,g9)
    c: Coincident(g13,g14)
    c: Perpendicular(g13,g9)
    c: Perpendicular(g14,g9)
    c: DistanceY(g5) = -281.46
    c: Coincident(g10,g15)
    c: Vertical(g15)
    c: Coincident(g15,g16)
    c: Coincident(g16,g17)
    c: Coincident(g17,g11)
    c: Coincident(g12,g18)
    c: Vertical(g18)
    c: Coincident(g18,g19)
    c: Coincident(g19,g20)
    c: Coincident(g20,g13)
    c: Parallel(g19,g16)
    c: Parallel(g16,g1)
    c: Vertical(g17)
    c: DistanceX(g11,g11) = 19
    c: PointOnObject(g16,g19)
    c: DistanceY(g18,g18) = 2
    c: Vertical(g20)
    c: Coincident(g21,g8)
    c: Coincident(g21,g15)
    c: Coincident(g22,g16)
    c: Coincident(g22,g18)
    c: Horizontal(g22)
FEATURE [PartDesign::Pad] Pad051
  BaseFeature = -> Pad041
  Direction = (0,0,1)
  Length = 30
  Length2 = 10
  Profile = -> Sketch093
  ReferenceAxis = -> Sketch093 [N_Axis]
  Refine = true
  Suppressed = false
  Type = 0
FEATURE [PartDesign::Plane] DatumPlane022
  AttachmentOffset = pos=(0,0,31) rot=(0,0,1;0rad)
  AttachmentSupport = -> [DatumPlane020]
  Length = 698.227
  MapMode = 5
  Placement = pos=(0,0,34) rot=(0,0,1;0rad)
  ResizeMode = 0
  Width = 412.39
FEATURE [Sketcher::SketchObject] Sketch095  label="cut at side for ribbon cable"
  ArcFitTolerance = 1e-06
  AttachmentSupport = -> [DatumPlane022]
  FullyConstrained = false
  MakeInternals = false
  MapMode = 5
  Placement = pos=(0,0,34) rot=(0,0,1;0rad)
  sketch-geometry (4):
    g0: LineSegment [constr] StartX=527.467 StartY=-273.043 StartZ=0 EndX=527.467 EndY=-297.368 EndZ=0
    g1: LineSegment [constr] StartX=527.467 StartY=-297.368 StartZ=0 EndX=535.467 EndY=-297.368 EndZ=0
    g2: LineSegment [constr] StartX=535.467 StartY=-297.368 StartZ=0 EndX=535.467 EndY=-273.043 EndZ=0
    g3: LineSegment [constr] StartX=535.467 StartY=-273.043 StartZ=0 EndX=527.467 EndY=-273.043 EndZ=0
  constraints (9):
    c: Coincident(g0,g1)
    c: Coincident(g1,g2)
    c: Coincident(g2,g3)
    c: Coincident(g3,g0)
    c: Vertical(g0)
    c: Vertical(g2)
    c: Horizontal(g1)
    c: Horizontal(g3)
    c: Distance(g0,g2) = 8
FEATURE [PartDesign::Pocket] Pocket041
  BaseFeature = -> Pad051
  Direction = (0,0,-1)
  Length = 10
  Length2 = 5
  Midplane = true
  Profile = -> Sketch079 [Edge15,Edge14]
  ReferenceAxis = -> Sketch079 [N_Axis]
  Refine = true
  Suppressed = false
  Type = 0
FEATURE [PartDesign::Pocket] Pocket035
  BaseFeature = -> Pocket041
  Direction = (0,0,-1)
  Length = 5
  Length2 = 5
  Profile = -> Sketch082
  ReferenceAxis = -> Sketch082 [N_Axis]
  Refine = true
  Reversed = true
  Suppressed = false
  Type = 0
FEATURE [PartDesign::Plane] DatumPlane021
  AttachmentSupport = -> [Pocket035]
  Length = 652.217
  MapMode = 5
  Placement = pos=(3.1038,-283.809,0) rot=(-0.003866,0.707101,0.707101;3.14933rad)
  ResizeMode = 0
  Width = 102.301
FEATURE [Sketcher::SketchObject] Sketch083
  ArcFitTolerance = 1e-06
  AttachmentSupport = -> [DatumPlane021]
  FullyConstrained = true
  MakeInternals = false
  MapMode = 5
  Placement = pos=(3.1038,-283.809,0) rot=(-0.003866,0.707101,0.707101;3.14933rad)
  expr: Constraints[4] = <<components>>.m3_hole - 1.3
  sketch-geometry (15):
    g0: LineSegment [constr] StartX=-549.7 StartY=9.5 StartZ=0 EndX=-528.7 EndY=9.5 EndZ=0
    g1: Circle CenterX=-549.7 CenterY=9.5 CenterZ=0 NormalX=0 NormalY=0 NormalZ=1 AngleXU=0 Radius=1.1
    g2: Circle CenterX=-528.7 CenterY=9.5 CenterZ=0 NormalX=0 NormalY=0 NormalZ=1 AngleXU=0 Radius=1.1
    g3: LineSegment [constr] StartX=-549.7 StartY=9.5 StartZ=0 EndX=-563.7 EndY=9.5 EndZ=0
    g4: LineSegment StartX=-537 StartY=19.2 StartZ=0 EndX=-537 EndY=11.7 EndZ=0
    g5: LineSegment StartX=-537 StartY=11.7 StartZ=0 EndX=-520.4 EndY=11.7 EndZ=0
    g6: LineSegment StartX=-520.4 StartY=11.7 StartZ=0 EndX=-520.4 EndY=19.2 EndZ=0
    g7: LineSegment StartX=-520.4 StartY=19.2 StartZ=0 EndX=-537 EndY=19.2 EndZ=0
    g8: LineSegment [constr] StartX=-528.7 StartY=9.5 StartZ=0 EndX=-528.7 EndY=19.2 EndZ=0
    g9: LineSegment [constr] StartX=-549.7 StartY=9.5 StartZ=0 EndX=-549.7 EndY=15.45 EndZ=0
    g10: LineSegment StartX=-559.2 StartY=11.7 StartZ=0 EndX=-540.2 EndY=11.7 EndZ=0
    g11: LineSegment StartX=-540.2 StartY=11.7 StartZ=0 EndX=-540.2 EndY=19.2 EndZ=0
    g12: LineSegment StartX=-540.2 StartY=19.2 StartZ=0 EndX=-559.2 EndY=19.2 EndZ=0
    g13: LineSegment StartX=-559.2 StartY=19.2 StartZ=0 EndX=-559.2 EndY=11.7 EndZ=0
    g14: GeomPoint [constr] X=-549.7 Y=15.45 Z=0
  constraints (40):
    c: Horizontal(g0)
    c: Coincident(g1,g0)
    c: Coincident(g2,g0)
    c: Equal(g1,g2)
    c: Diameter(g2) = 2.2
    c: Coincident(g3,g0)
    c: Horizontal(g3)
    c: Distance(g3) = 14
    c: Distance(g3,g0) = 35
    c: Coincident(g4,g5)
    c: Coincident(g5,g6)
    c: Coincident(g6,g7)
    c: Coincident(g7,g4)
    c: Vertical(g4)
    c: Vertical(g6)
    c: Horizontal(g5)
    c: Horizontal(g7)
    c: Distance(g4,g6) = 16.6
    c: Distance(g5,g7) = 7.5
    c: Coincident(g8,g0)
    c: Symmetric(g7,g7,g8)
    c: Vertical(g8)
    c: DistanceX(g4) = -537
    c: DistanceY(g4) = 19.2
    c: DistanceY(g3) = 9.5
    c: Coincident(g9,g0)
    c: Vertical(g9)
    c: Coincident(g10,g11)
    c: Coincident(g11,g12)
    c: Coincident(g12,g13)
    c: Coincident(g13,g10)
    c: Horizontal(g10)
    c: Horizontal(g12)
    c: Vertical(g11)
    c: Vertical(g13)
    c: Symmetric(g12,g10,g14)
    c: Distance(g11,g13) = 19
    c: Distance(g10,g12) = 7.5
    c: Coincident(g14,g9)
    c: PointOnObject(g4,g10)
FEATURE [PartDesign::Pocket] Pocket036
  BaseFeature = -> Pocket035
  Direction = (0.0109356,-0.99994,0)
  Length = 7
  Length2 = 5
  Profile = -> Sketch083
  ReferenceAxis = -> Sketch083 [N_Axis]
  Refine = true
  Suppressed = false
  Type = 0
FEATURE [PartDesign::Pad] Pad042
  BaseFeature = -> Pocket036
  Direction = (0,0,1)
  Length = 10
  Length2 = 10
  Profile = -> Sketch084
  ReferenceAxis = -> Sketch084 [N_Axis]
  Refine = true
  Suppressed = false
  Type = 0
FEATURE [Sketcher::SketchObject] Sketch096
  ArcFitTolerance = 1e-06
  AttachmentSupport = -> [DatumPlane021]
  FullyConstrained = false
  MakeInternals = false
  MapMode = 5
  Placement = pos=(3.1038,-283.809,0) rot=(-0.003866,0.707101,0.707101;3.14933rad)
  sketch-geometry (8):
    g0: LineSegment StartX=-568.28 StartY=26.01 StartZ=0 EndX=-568.28 EndY=9 EndZ=0
    g1: LineSegment StartX=-568.28 StartY=9 StartZ=0 EndX=-553.192 EndY=9 EndZ=0
    g2: LineSegment StartX=-509.954 StartY=9 StartZ=0 EndX=-509.954 EndY=26.01 EndZ=0
    g3: LineSegment StartX=-509.954 StartY=26.01 StartZ=0 EndX=-568.28 EndY=26.01 EndZ=0
    g4: ArcOfCircle CenterX=-549.77 CenterY=9 CenterZ=0 NormalX=0 NormalY=0 NormalZ=1 AngleXU=0 Radius=3.42249 StartAngle=3.14159 EndAngle=6.28319
    g5: ArcOfCircle CenterX=-528.77 CenterY=9 CenterZ=0 NormalX=0 NormalY=0 NormalZ=1 AngleXU=0 Radius=3.42249 StartAngle=3.14159 EndAngle=6.28319
    g6: LineSegment StartX=-546.348 StartY=9 StartZ=0 EndX=-532.192 EndY=9 EndZ=0
    g7: LineSegment StartX=-525.348 StartY=9 StartZ=0 EndX=-509.954 EndY=9 EndZ=0
  constraints (26):
    c: Coincident(g0,g1)
    c: Coincident(g7,g2)
    c: Coincident(g2,g3)
    c: Coincident(g3,g0)
    c: Vertical(g0)
    c: Vertical(g2)
    c: Horizontal(g1)
    c: Horizontal(g3)
    c: DistanceX(g0) = -568.28
    c: DistanceY(g0) = 26.01
    c: DistanceY(g0) = 9
    c: PointOnObject(g4,g1)
    c: PointOnObject(g5,g6)
    c: Equal(g5,g4)
    c: PointOnObject(g4,g6)
    c: PointOnObject(g5,g7)
    c: Coincident(g1,g4)
    c: PointOnObject(g6,g4)
    c: Coincident(g6,g5)
    c: PointOnObject(g7,g5)
    c: Horizontal(g6)
    c: DistanceX(g4) = -549.77
    c: DistanceX(g5) = -528.77
    c: Horizontal(g7)
    c: PointOnObject(g5,g6)
    c: PointOnObject(g1,g6)
FEATURE [PartDesign::Pocket] Pocket042
  BaseFeature = -> Pad042
  Direction = (0.0109356,-0.99994,0)
  Length = 3.7
  Length2 = 5
  Profile = -> Sketch096
  ReferenceAxis = -> Sketch096 [N_Axis]
  Refine = true
  Suppressed = false
  Type = 0
FEATURE [PartDesign::Chamfer] Chamfer011
  Angle = 45
  Base = -> Pocket042 [Edge161,Edge163]
  BaseFeature = -> Pocket042
  ChamferType = 0
  FlipDirection = false
  Refine = true
  Size = 0.5
  Size2 = 1
  SupportTransform = false
  Suppressed = false
  UseAllEdges = false
FEATURE [PartDesign::Chamfer] Chamfer012
  Angle = 45
  Base = -> Chamfer011 [Edge19,Edge15]
  BaseFeature = -> Chamfer011
  ChamferType = 0
  FlipDirection = false
  Refine = true
  Size = 2
  Size2 = 1
  SupportTransform = false
  Suppressed = false
  UseAllEdges = false
FEATURE [PartDesign::Chamfer] Chamfer013
  Angle = 45
  Base = -> Chamfer012 [Edge194,Edge198,Edge201,Edge200,Edge196,Edge192,Edge188,Edge190]
  BaseFeature = -> Chamfer012
  ChamferType = 0
  FlipDirection = false
  Refine = true
  Size = 2.4
  Size2 = 1
  SupportTransform = false
  Suppressed = false
  UseAllEdges = false
FEATURE [PartDesign::Chamfer] Chamfer014
  Angle = 45
  Base = -> Chamfer013 [Edge7]
  BaseFeature = -> Chamfer013
  ChamferType = 0
  FlipDirection = false
  Refine = true
  Size = 1.29
  Size2 = 1
  SupportTransform = false
  Suppressed = false
  UseAllEdges = false
FEATURE [PartDesign::Body] Body018
  AllowCompound = false
  Group = -> [Sketch079,Pad039,Sketch080,Pad040,Sketch081,Pad041,Pad051,Pocket041,Sketch082,DatumPlane020,Pocket035,DatumPlane021,Sketch083,Pocket036,Sketch084,Pad042,Pocket042,Sketch093,Chamfer011,Sketch095,DatumPlane022,Sketch096,Chamfer012,Chamfer013,Chamfer014]
  Origin = -> Origin039
  Tip = -> Chamfer014
COMPONENT P7 — recipe-attached ("LEFT_END001", modeled in this document).
Construction recipe (the document's own serialized feature program — sketch geometry with constraints, then the solid features built on it; lengths are millimeters unless a unit is written):

FEATURE [PartDesign::Plane] DatumPlane015
  AttachmentOffset = pos=(0,0,20) rot=(0,0,1;0rad)
  AttachmentSupport = -> [XY_Plane035]
  Length = 120.269
  MapMode = 5
  Placement = pos=(0,0,20) rot=(0,0,1;0rad)
  ResizeMode = 0
  Width = 284.769
  expr: .AttachmentOffset.Base.z = <<choices>>.base_max_thickness
FEATURE [Sketcher::SketchObject] Sketch068
  ArcFitTolerance = 1e-06
  AttachmentSupport = -> [DatumPlane015]
  FullyConstrained = false
  MakeInternals = false
  MapMode = 5
  Placement = pos=(0,0,20) rot=(0,0,1;0rad)
  expr: Constraints[22] = <<choices>>.corner
  expr: Constraints[23] = <<components>>.m3_hole
  expr: Constraints[24] = <<choices>>.screwhole_edge_margin
  expr: Constraints[26] = <<choices>>.screwhole_edge_margin
  expr: Constraints[7] = <<components>>.frame_h
  sketch-geometry (31):
    g0: LineSegment StartX=1 StartY=0 StartZ=0 EndX=65 EndY=0 EndZ=0
    g1: LineSegment [constr] StartX=65 StartY=0 StartZ=0 EndX=65 EndY=228.5 EndZ=0
    g2: LineSegment StartX=64 StartY=229.5 StartZ=0 EndX=1 EndY=229.5 EndZ=0
    g3: LineSegment StartX=0 StartY=228.5 StartZ=0 EndX=0 EndY=1 EndZ=0
    g4: ArcOfCircle CenterX=1 CenterY=228.5 CenterZ=0 NormalX=0 NormalY=0 NormalZ=1 AngleXU=0 Radius=1 StartAngle=1.5708 EndAngle=3.14159
    g5: GeomPoint [constr] X=0 Y=229.5 Z=0
    g6: ArcOfCircle CenterX=64 CenterY=228.5 CenterZ=0 NormalX=0 NormalY=0 NormalZ=1 AngleXU=0 Radius=1 StartAngle=-1.33e-14 EndAngle=1.5708
    g7: GeomPoint [constr] X=65 Y=229.5 Z=0
    g8: ArcOfCircle CenterX=1 CenterY=1 CenterZ=0 NormalX=0 NormalY=0 NormalZ=1 AngleXU=0 Radius=1 StartAngle=3.14159 EndAngle=4.71239
    g9: GeomPoint [constr] X=0 Y=0 Z=0
    g10: Circle CenterX=5 CenterY=8 CenterZ=0 NormalX=0 NormalY=0 NormalZ=1 AngleXU=0 Radius=1.75
    g11: Circle CenterX=5 CenterY=221.5 CenterZ=0 NormalX=0 NormalY=0 NormalZ=1 AngleXU=0 Radius=1.75
    g12: LineSegment StartX=65 StartY=228.5 StartZ=0 EndX=65 EndY=186 EndZ=0
    g13: LineSegment StartX=65 StartY=186 StartZ=0 EndX=3 EndY=186 EndZ=0
    g14: LineSegment StartX=3 StartY=186 StartZ=0 EndX=3 EndY=12 EndZ=0
    g15: LineSegment StartX=65 StartY=0 StartZ=0 EndX=65 EndY=3 EndZ=0
    g16: LineSegment StartX=65 StartY=3 StartZ=0 EndX=9 EndY=3 EndZ=0
    g17: LineSegment StartX=9 StartY=3 StartZ=0 EndX=9 EndY=12 EndZ=0
    g18: LineSegment StartX=9 StartY=12 StartZ=0 EndX=3 EndY=12 EndZ=0
    g19: LineSegment StartX=3 StartY=192 StartZ=0 EndX=40.5999 EndY=192 EndZ=0
    g20: LineSegment StartX=62 StartY=213.4 StartZ=0 EndX=62 EndY=216.254 EndZ=0
    g21: LineSegment StartX=51.754 StartY=226.5 StartZ=0 EndX=10 EndY=226.5 EndZ=0
    g22: LineSegment StartX=10 StartY=226.5 StartZ=0 EndX=10 EndY=216.5 EndZ=0
    g23: LineSegment StartX=10 StartY=216.5 StartZ=0 EndX=3 EndY=216.5 EndZ=0
    g24: LineSegment StartX=3 StartY=216.5 StartZ=0 EndX=3 EndY=192 EndZ=0
    g25: ArcOfCircle [constr] CenterX=51.754 CenterY=216.254 CenterZ=0 NormalX=0 NormalY=0 NormalZ=1 AngleXU=0 Radius=10.246 StartAngle=3e-16 EndAngle=1.5708
    g26: GeomPoint [constr] X=62 Y=226.5 Z=0
    g27: LineSegment StartX=62 StartY=216.254 StartZ=0 EndX=51.754 EndY=226.5 EndZ=0
    g28: ArcOfCircle [constr] CenterX=40.5999 CenterY=213.4 CenterZ=0 NormalX=0 NormalY=0 NormalZ=1 AngleXU=0 Radius=21.4001 StartAngle=4.71239 EndAngle=6.28319
    g29: GeomPoint [constr] X=62 Y=192 Z=0
    g30: LineSegment StartX=40.5999 StartY=192 StartZ=0 EndX=62 EndY=213.4 EndZ=0
  constraints (77):
    c: Coincident(g0,g1)
    c: Horizontal(g0)
    c: Horizontal(g2)
    c: Vertical(g1)
    c: Vertical(g3)
    c: Distance(g1,g9) = 65
    c: Coincident(g9,g-1)
    c: DistanceY(g9,g5) = 229.5
    c: PointOnObject(g5,g2)
    c: PointOnObject(g5,g3)
    c: Tangent(g2,g4) = -1.5708
    c: Tangent(g3,g4) = -1.5708
    c: PointOnObject(g7,g1)
    c: PointOnObject(g7,g2)
    c: Tangent(g1,g6) = -1.5708
    c: Tangent(g2,g6) = -1.5708
    c: PointOnObject(g9,g3)
    c: PointOnObject(g9,g0)
    c: Tangent(g3,g8) = -1.5708
    c: Tangent(g0,g8) = -1.5708
    c: Equal(g8,g4)
    c: Equal(g4,g6)
    c: Radius(g4) = 1
    c: Diameter(g10) = 3.5
    c: DistanceX(g10) = 5
    c: DistanceY(g10) = 8
    c: DistanceX(g11) = 5
    c: Distance(g11,g2) = 8
    c: Equal(g10,g11)
    c: Coincident(g12,g1)
    c: PointOnObject(g12,g1)
    c: Coincident(g13,g12)
    c: Horizontal(g13)
    c: Coincident(g14,g13)
    c: Vertical(g14)
    c: Distance(g15) = 3
    c: Coincident(g15,g0)
    c: PointOnObject(g15,g1)
    c: Coincident(g16,g15)
    c: Horizontal(g16)
    c: Coincident(g17,g16)
    c: Vertical(g17)
    c: Coincident(g18,g17)
    c: Horizontal(g18)
    c: Coincident(g14,g18)
    c: DistanceY(g14) = 12
    c: DistanceX(g17) = 9
    c: Horizontal(g19)
    c: Vertical(g20)
    c: Horizontal(g21)
    c: Coincident(g21,g22)
    c: Vertical(g22)
    c: Coincident(g22,g23)
    c: Horizontal(g23)
    c: Coincident(g23,g24)
    c: Coincident(g24,g19)
    c: Vertical(g24)
    c: Distance(g21,g2) = 3
    c: DistanceX(g22) = 10
    c: Distance(g22,g2) = 13
    c: DistanceX(g19) = 3
    c: Distance(g29,g12) = 3
    c: Distance(g13,g3) = 3
    c: Distance(g13,g19) = 6
    c: DistanceY(g13) = 186
    c: PointOnObject(g26,g21)
    c: PointOnObject(g26,g20)
    c: Tangent(g21,g25) = -1.5708
    c: Tangent(g20,g25) = -1.5708
    c: Coincident(g27,g21)
    c: Coincident(g27,g20)
    c: PointOnObject(g29,g19)
    c: PointOnObject(g29,g20)
    c: Tangent(g19,g28) = -1.5708
    c: Tangent(g20,g28) = -1.5708
    c: Coincident(g30,g19)
    c: Coincident(g30,g20)
FEATURE [PartDesign::Pad] Pad032
  Direction = (0,0,1)
  Length = 38
  Length2 = 10
  Placement = pos=(0,0,20) rot=(0,0,1;0rad)
  Profile = -> Sketch068
  ReferenceAxis = -> Sketch068 [N_Axis]
  Refine = true
  Suppressed = false
  Type = 0
  expr: Length = <<choices>>.exit_height - <<choices>>.base_max_thickness + 3
FEATURE [Sketcher::SketchObject] Sketch069
  ArcFitTolerance = 1e-06
  AttachmentSupport = -> [DatumPlane015]
  FullyConstrained = true
  MakeInternals = false
  MapMode = 5
  Placement = pos=(0,0,20) rot=(0,0,1;0rad)
  expr: Constraints[10] = <<components>>.m3_hole
  expr: Constraints[12] = <<components>>.frame_h - 8
  expr: Constraints[7] = <<components>>.frame_h - 3
  sketch-geometry (13):
    g0: LineSegment StartX=0 StartY=226.5 StartZ=0 EndX=0 EndY=188 EndZ=0
    g1: LineSegment StartX=10 StartY=226.5 StartZ=0 EndX=0 EndY=226.5 EndZ=0
    g2: Circle CenterX=5 CenterY=221.5 CenterZ=0 NormalX=0 NormalY=0 NormalZ=1 AngleXU=0 Radius=1.75
    g3: LineSegment [constr] StartX=10 StartY=188 StartZ=0 EndX=10 EndY=216.5 EndZ=0
    g4: LineSegment StartX=0 StartY=188 StartZ=0 EndX=3 EndY=188 EndZ=0
    g5: LineSegment [constr] StartX=3 StartY=188 StartZ=0 EndX=10 EndY=188 EndZ=0
    g6: LineSegment StartX=10 StartY=216.5 StartZ=0 EndX=3 EndY=216.5 EndZ=0
    g7: LineSegment StartX=3 StartY=216.5 StartZ=0 EndX=3 EndY=188 EndZ=0
    g8: LineSegment StartX=10 StartY=216.5 StartZ=0 EndX=10 EndY=224.5 EndZ=0
    g9: LineSegment [constr] StartX=10 StartY=224.5 StartZ=0 EndX=10 EndY=226.5 EndZ=0
    g10: LineSegment StartX=10 StartY=224.5 StartZ=0 EndX=55 EndY=224.5 EndZ=0
    g11: LineSegment StartX=55 StartY=224.5 StartZ=0 EndX=55 EndY=226.5 EndZ=0
    g12: LineSegment StartX=55 StartY=226.5 StartZ=0 EndX=10 EndY=226.5 EndZ=0
  constraints (37):
    c: Coincident(g0,g4)
    c: Coincident(g5,g3)
    c: Coincident(g9,g1)
    c: Coincident(g1,g0)
    c: Vertical(g0)
    c: Horizontal(g1)
    c: PointOnObject(g0,g-2)
    c: DistanceY(g0) = 226.5
    c: DistanceX(g1,g1) = 10
    c: DistanceY(g0) = 188
    c: Diameter(g2) = 3.5
    c: DistanceX(g2) = 5
    c: DistanceY(g2) = 221.5
    c: Coincident(g3,g8)
    c: Vertical(g3)
    c: Coincident(g4,g5)
    c: Horizontal(g4)
    c: Horizontal(g5)
    c: Coincident(g3,g6)
    c: Horizontal(g6)
    c: Coincident(g6,g7)
    c: Coincident(g7,g4)
    c: Vertical(g7)
    c: DistanceX(g4,g4) = 3
    c: DistanceY(g8,g9) = 10
    c: Coincident(g8,g9)
    c: Vertical(g8)
    c: Vertical(g9)
    c: Coincident(g8,g10)
    c: Horizontal(g10)
    c: Coincident(g10,g11)
    c: Vertical(g11)
    c: Coincident(g11,g12)
    c: Coincident(g12,g1)
    c: Horizontal(g12)
    c: DistanceY(g11,g11) = 2
    c: DistanceX(g11) = 55
FEATURE [PartDesign::Pad] Pad033
  BaseFeature = -> Pad032
  Direction = (0,0,1)
  Length = 17
  Length2 = 10
  Placement = pos=(0,0,20) rot=(0,0,1;0rad)
  Profile = -> Sketch069
  ReferenceAxis = -> Sketch069 [N_Axis]
  Refine = true
  Reversed = true
  Suppressed = false
  Type = 0
  expr: Length = <<choices>>.base_max_thickness - 3
FEATURE [Sketcher::SketchObject] Sketch070
  ArcFitTolerance = 1e-06
  AttachmentSupport = -> [YZ_Plane035]
  FullyConstrained = true
  MakeInternals = false
  MapMode = 5
  Placement = pos=(0,0,0) rot=(0.57735,0.57735,0.57735;2.0944rad)
  expr: Constraints[1] = <<components>>.m3_hole
  sketch-geometry (16):
    g0: Circle CenterX=204.62 CenterY=50 CenterZ=0 NormalX=0 NormalY=0 NormalZ=1 AngleXU=0 Radius=1.75
    g1: Circle CenterX=204.62 CenterY=10 CenterZ=0 NormalX=0 NormalY=0 NormalZ=1 AngleXU=0 Radius=1.75
    g2: LineSegment [constr] StartX=204.62 StartY=50 StartZ=0 EndX=204.62 EndY=10 EndZ=0
    g3: LineSegment StartX=194.62 StartY=14.55 StartZ=0 EndX=214.62 EndY=14.55 EndZ=0
    g4: LineSegment StartX=215.62 StartY=15.55 StartZ=0 EndX=215.62 EndY=44.45 EndZ=0
    g5: LineSegment StartX=214.62 StartY=45.45 StartZ=0 EndX=194.62 EndY=45.45 EndZ=0
    g6: LineSegment StartX=193.62 StartY=44.45 StartZ=0 EndX=193.62 EndY=15.55 EndZ=0
    g7: GeomPoint [constr] X=204.62 Y=30 Z=0
    g8: ArcOfCircle CenterX=194.62 CenterY=44.45 CenterZ=0 NormalX=0 NormalY=0 NormalZ=1 AngleXU=0 Radius=1 StartAngle=1.5708 EndAngle=3.14159
    g9: GeomPoint [constr] X=193.62 Y=45.45 Z=0
    g10: ArcOfCircle CenterX=194.62 CenterY=15.55 CenterZ=0 NormalX=0 NormalY=0 NormalZ=1 AngleXU=0 Radius=1 StartAngle=3.14159 EndAngle=4.71239
    g11: GeomPoint [constr] X=193.62 Y=14.55 Z=0
    g12: ArcOfCircle CenterX=214.62 CenterY=15.55 CenterZ=0 NormalX=0 NormalY=0 NormalZ=1 AngleXU=0 Radius=1 StartAngle=4.71239 EndAngle=6.28319
    g13: GeomPoint [constr] X=215.62 Y=14.55 Z=0
    g14: ArcOfCircle CenterX=214.62 CenterY=44.45 CenterZ=0 NormalX=0 NormalY=0 NormalZ=1 AngleXU=0 Radius=1 StartAngle=-3.6e-15 EndAngle=1.5708
    g15: GeomPoint [constr] X=215.62 Y=45.45 Z=0
  constraints (36):
    c: Equal(g0,g1)
    c: Diameter(g0) = 3.5
    c: Coincident(g2,g0)
    c: Coincident(g2,g1)
    c: Vertical(g2)
    c: DistanceY(g2,g2) = 40
    c: Horizontal(g3)
    c: Horizontal(g5)
    c: Vertical(g4)
    c: Vertical(g6)
    c: Symmetric(g15,g11,g7)
    c: Distance(g13,g11) = 22
    c: Distance(g11,g9) = 30.9
    c: Symmetric(g2,g2,g7)
    c: DistanceY(g1) = 10
    c: PointOnObject(g9,g5)
    c: PointOnObject(g9,g6)
    c: Tangent(g5,g8) = -1.5708
    c: Tangent(g6,g8) = -1.5708
    c: PointOnObject(g11,g6)
    c: PointOnObject(g11,g3)
    c: Tangent(g6,g10) = -1.5708
    c: Tangent(g3,g10) = -1.5708
    c: PointOnObject(g13,g3)
    c: PointOnObject(g13,g4)
    c: Tangent(g3,g12) = -1.5708
    c: Tangent(g4,g12) = -1.5708
    c: PointOnObject(g15,g4)
    c: PointOnObject(g15,g5)
    c: Tangent(g4,g14) = -1.5708
    c: Tangent(g5,g14) = -1.5708
    c: DistanceX(g7) = 204.62
    c: Equal(g12,g14)
    c: Equal(g14,g8)
    c: Equal(g8,g10)
    c: Radius(g10) = 1
FEATURE [PartDesign::Plane] DatumPlane017
  AttachmentOffset = pos=(0,0,-229.5) rot=(0,0,1;0rad)
  AttachmentSupport = -> [XZ_Plane035]
  Length = 107.286
  MapMode = 5
  Placement = pos=(0,229.5,-5.1e-14) rot=(1,0,0;1.5708rad)
  ResizeMode = 0
  Width = 100.286
  expr: .AttachmentOffset.Base.z = -<<components>>.frame_h
FEATURE [PartDesign::Plane] DatumPlane018
  AttachmentOffset = pos=(0,0,-188) rot=(0,0,1;0rad)
  AttachmentSupport = -> [XZ_Plane035]
  Length = 107.286
  MapMode = 5
  Placement = pos=(0,188,-4.17e-14) rot=(1,0,0;1.5708rad)
  ResizeMode = 0
  Width = 100.286
FEATURE [Sketcher::SketchObject] Sketch072
  ArcFitTolerance = 1e-06
  AttachmentSupport = -> [DatumPlane017]
  FullyConstrained = true
  MakeInternals = false
  MapMode = 5
  Placement = pos=(0,229.5,-5.1e-14) rot=(1,0,0;1.5708rad)
  expr: Constraints[1] = 65 / 2
  expr: Constraints[2] = (<<choices>>.exit_height - <<choices>>.base_max_thickness) * 0.5 + <<choices>>.base_max_thickness + 7.5
  sketch-geometry (1):
    g0: Circle CenterX=32.5 CenterY=45 CenterZ=0 NormalX=0 NormalY=0 NormalZ=1 AngleXU=0 Radius=8.15
  constraints (3):
    c: Diameter(g0) = 16.3
    c: DistanceX(g-1,g0) = 32.5
    c: DistanceY(g0) = 45
FEATURE [PartDesign::Pad] Pad034
  BaseFeature = -> Pad033
  Direction = (0,0,1)
  Length = 3
  Length2 = 10
  Placement = pos=(0,0,20) rot=(0,0,1;0rad)
  Profile = -> Sketch069
  ReferenceAxis = -> Sketch069 [N_Axis]
  Refine = true
  Suppressed = false
  Type = 0
FEATURE [PartDesign::Pocket] Pocket031
  BaseFeature = -> Pad034
  Direction = (-1,0,0)
  Length = 5
  Length2 = 5
  Placement = pos=(0,0,20) rot=(0,0,1;0rad)
  Profile = -> Sketch070
  ReferenceAxis = -> Sketch070 [N_Axis]
  Refine = true
  Reversed = true
  Suppressed = false
  Type = 0
FEATURE [PartDesign::Pocket] Pocket033
  BaseFeature = -> Pocket031
  Direction = (0,1,-2e-16)
  Length = 5
  Length2 = 5
  Placement = pos=(0,0,20) rot=(0,0,1;0rad)
  Profile = -> Sketch072
  ReferenceAxis = -> Sketch072 [N_Axis]
  Refine = true
  Reversed = true
  Suppressed = false
  Type = 0
FEATURE [Sketcher::SketchObject] Sketch073
  ArcFitTolerance = 1e-06
  AttachmentSupport = -> [DatumPlane018]
  FullyConstrained = false
  MakeInternals = false
  MapMode = 5
  Placement = pos=(0,188,-4.17e-14) rot=(1,0,0;1.5708rad)
  sketch-geometry (5):
    g0: LineSegment StartX=8.21147 StartY=51.4718 StartZ=0 EndX=8.21147 EndY=26.7757 EndZ=0
    g1: LineSegment StartX=8.21147 StartY=26.7757 StartZ=0 EndX=41.1685 EndY=26.7757 EndZ=0
    g2: LineSegment StartX=41.1685 StartY=26.7757 StartZ=0 EndX=57.8674 EndY=40.0932 EndZ=0
    g3: LineSegment StartX=57.8674 StartY=40.0932 StartZ=0 EndX=40.5009 EndY=51.4718 EndZ=0
    g4: LineSegment StartX=40.5009 StartY=51.4718 StartZ=0 EndX=8.21147 EndY=51.4718 EndZ=0
  constraints (8):
    c: Vertical(g0)
    c: Coincident(g0,g1)
    c: Horizontal(g1)
    c: Coincident(g1,g2)
    c: Coincident(g2,g3)
    c: Coincident(g3,g4)
    c: Horizontal(g4)
    c: Coincident(g4,g0)
FEATURE [PartDesign::Pocket] Pocket034
  BaseFeature = -> Pocket033
  Direction = (0,1,-2e-16)
  Length = 33
  Length2 = 5
  Midplane = true
  Placement = pos=(0,0,20) rot=(0,0,1;0rad)
  Profile = -> Sketch073
  ReferenceAxis = -> Sketch073 [N_Axis]
  Refine = true
  Suppressed = false
  Type = 0
FEATURE [PartDesign::Chamfer] Chamfer007
  Angle = 45
  Base = -> Pocket034 [Edge72,Edge81]
  BaseFeature = -> Pocket034
  ChamferType = 0
  FlipDirection = false
  Placement = pos=(0,0,20) rot=(0,0,1;0rad)
  Refine = true
  Size = 1.75
  Size2 = 1
  SupportTransform = false
  Suppressed = false
  UseAllEdges = false
FEATURE [Sketcher::SketchObject] Sketch092
  ArcFitTolerance = 1e-06
  AttachmentSupport = -> [DatumPlane015]
  FullyConstrained = false
  MakeInternals = false
  MapMode = 5
  Placement = pos=(0,0,20) rot=(0,0,1;0rad)
  sketch-geometry (6):
    g0: LineSegment StartX=59.5 StartY=2.95 StartZ=0 EndX=59.5 EndY=5.35 EndZ=0
    g1: LineSegment StartX=59.5 StartY=5.35 StartZ=0 EndX=64.5503 EndY=5.35 EndZ=0
    g2: LineSegment StartX=64.5503 StartY=5.35 StartZ=0 EndX=64.5503 EndY=7.35 EndZ=0
    g3: LineSegment StartX=64.5503 StartY=7.35 StartZ=0 EndX=57.1811 EndY=7.35 EndZ=0
    g4: LineSegment StartX=57.1811 StartY=7.35 StartZ=0 EndX=43.3859 EndY=2.95 EndZ=0
    g5: LineSegment StartX=43.3859 StartY=2.95 StartZ=0 EndX=59.5 EndY=2.95 EndZ=0
  constraints (15):
    c: Vertical(g0)
    c: Coincident(g0,g1)
    c: Horizontal(g1)
    c: Coincident(g1,g2)
    c: Vertical(g2)
    c: Coincident(g2,g3)
    c: Horizontal(g3)
    c: Coincident(g3,g4)
    c: Coincident(g4,g5)
    c: Coincident(g5,g0)
    c: Horizontal(g5)
    c: DistanceY(g0) = 2.95
    c: DistanceX(g0) = 59.5
    c: DistanceY(g0,g0) = 2.4
    c: DistanceY(g2,g2) = 2
FEATURE [PartDesign::Pad] Pad050
  BaseFeature = -> Chamfer007
  Direction = (0,0,1)
  Length = 30
  Length2 = 10
  Placement = pos=(0,0,20) rot=(0,0,1;0rad)
  Profile = -> Sketch092
  ReferenceAxis = -> Sketch092 [N_Axis]
  Refine = true
  Suppressed = false
  Type = 0
FEATURE [PartDesign::Body] Body016
  AllowCompound = false
  Group = -> [DatumPlane015,Sketch068,Pad032,Sketch069,Pad033,Pad034,Sketch070,Pocket031,DatumPlane017,DatumPlane018,Sketch072,Pocket033,Sketch073,Pocket034,Chamfer007,Sketch092,Pad050]
  Origin = -> Origin035
  Tip = -> Pad050
COMPONENT P8 — recipe-attached ("LEG_CLAMP001", modeled in this document).
Construction recipe (the document's own serialized feature program — sketch geometry with constraints, then the solid features built on it; lengths are millimeters unless a unit is written):

FEATURE [Sketcher::SketchObject] Sketch055
  ArcFitTolerance = 1e-06
  AttachmentSupport = -> [XY_Plane029]
  FullyConstrained = false
  MakeInternals = false
  MapMode = 5
  expr: Constraints[10] = <<components>>.m3_hole
  sketch-geometry (8):
    g0: LineSegment StartX=532.782 StartY=-279.207 StartZ=0 EndX=532.782 EndY=-400.207 EndZ=0
    g1: LineSegment StartX=532.782 StartY=-400.207 StartZ=0 EndX=542.782 EndY=-400.207 EndZ=0
    g2: LineSegment StartX=542.782 StartY=-400.207 StartZ=0 EndX=542.782 EndY=-279.207 EndZ=0
    g3: LineSegment StartX=542.782 StartY=-279.207 StartZ=0 EndX=532.782 EndY=-279.207 EndZ=0
    g4: LineSegment [constr] StartX=542.782 StartY=-290.207 StartZ=0 EndX=532.782 EndY=-290.207 EndZ=0
    g5: Circle CenterX=537.782 CenterY=-381.209 CenterZ=0 NormalX=0 NormalY=0 NormalZ=1 AngleXU=0 Radius=1.75
    g6: Circle CenterX=537.782 CenterY=-284.707 CenterZ=0 NormalX=0 NormalY=0 NormalZ=1 AngleXU=0 Radius=1.75
    g7: LineSegment [constr] StartX=537.782 StartY=-284.707 StartZ=0 EndX=537.782 EndY=-381.209 EndZ=0
  constraints (19):
    c: Coincident(g0,g1)
    c: Coincident(g1,g2)
    c: Coincident(g2,g3)
    c: Coincident(g3,g0)
    c: Vertical(g0)
    c: Vertical(g2)
    c: Horizontal(g1)
    c: Horizontal(g3)
    c: Horizontal(g4)
    c: Equal(g5,g6)
    c: Diameter(g6) = 3.5
    c: Coincident(g7,g6)
    c: Coincident(g7,g5)
    c: DistanceX(g4,g4) = 10
    c: Distance(g4,g3) = 11
    c: Symmetric(g4,g4,g7)
    c: DistanceY(g2,g2) = 121
    c: PointOnObject(g4,g2)
    c: PointOnObject(g4,g0)
FEATURE [PartDesign::Pad] Pad026
  Direction = (0,0,1)
  Length = 5
  Length2 = 10
  Profile = -> Sketch055
  ReferenceAxis = -> Sketch055 [N_Axis]
  Refine = true
  Suppressed = false
  Type = 0
FEATURE [Sketcher::SketchObject] Sketch056
  ArcFitTolerance = 1e-06
  AttachmentSupport = -> [YZ_Plane029]
  FullyConstrained = false
  MakeInternals = false
  MapMode = 5
  Placement = pos=(0,0,0) rot=(0.57735,0.57735,0.57735;2.0944rad)
  expr: Constraints[0] = <<choices>>.leg_axle_hole_dia
  expr: Constraints[8] = <<choices>>.leg_axle_hole_dia / 2
  sketch-geometry (5):
    g0: Circle CenterX=-392.256 CenterY=5 CenterZ=0 NormalX=0 NormalY=0 NormalZ=1 AngleXU=0 Radius=2.6
    g1: ArcOfCircle CenterX=-357.458 CenterY=5 CenterZ=0 NormalX=0 NormalY=0 NormalZ=1 AngleXU=0 Radius=2.6 StartAngle=1.5708 EndAngle=4.71239
    g2: ArcOfCircle CenterX=-296.003 CenterY=5 CenterZ=0 NormalX=0 NormalY=0 NormalZ=1 AngleXU=0 Radius=2.6 StartAngle=4.71239 EndAngle=7.85398
    g3: LineSegment StartX=-357.458 StartY=7.6 StartZ=0 EndX=-296.003 EndY=7.6 EndZ=0
    g4: LineSegment StartX=-357.458 StartY=2.4 StartZ=0 EndX=-296.003 EndY=2.4 EndZ=0
  constraints (10):
    c: Diameter(g0) = 5.2
    c: DistanceY(g0) = 5
    c: Tangent(g1,g3) = 1.5708
    c: Tangent(g1,g4) = -1.5708
    c: Tangent(g2,g3) = 1.5708
    c: Tangent(g2,g4) = -1.5708
    c: Equal(g1,g2)
    c: Horizontal(g3)
    c: Radius(g2) = 2.6
    c: DistanceY(g2) = 5
FEATURE [PartDesign::Pocket] Pocket026
  BaseFeature = -> Pad026
  Direction = (-1,0,0)
  Length = 5
  Length2 = 5
  Midplane = true
  Profile = -> Sketch056
  ReferenceAxis = -> Sketch056 [N_Axis]
  Refine = true
  Suppressed = false
  Type = 1
FEATURE [PartDesign::Chamfer] Chamfer002
  Angle = 45
  Base = -> Pocket026 [Edge15,Edge14]
  BaseFeature = -> Pocket026
  ChamferType = 0
  FlipDirection = false
  Refine = true
  Size = 1.75
  Size2 = 1
  SupportTransform = false
  Suppressed = false
  UseAllEdges = false
FEATURE [PartDesign::Body] Body013
  AllowCompound = false
  Group = -> [Sketch055,Pad026,Sketch056,Pocket026,Chamfer002]
  Origin = -> Origin029
  Tip = -> Chamfer002
COMPONENT P9 — recipe-attached ("MOTHERBOARD001", modeled in this document).
Construction recipe (the document's own serialized feature program — sketch geometry with constraints, then the solid features built on it; lengths are millimeters unless a unit is written):

FEATURE [Sketcher::SketchObject] Sketch004
  ArcFitTolerance = 1e-06
  AttachmentSupport = -> [XY_Plane005]
  FullyConstrained = true
  MakeInternals = false
  MapMode = 5
  expr: Constraints[10] = <<components>>.mb_h
  expr: Constraints[9] = <<components>>.mb_w
  sketch-geometry (12):
    g0: LineSegment StartX=0 StartY=0 StartZ=0 EndX=170 EndY=0 EndZ=0
    g1: LineSegment StartX=170 StartY=0 StartZ=0 EndX=170 EndY=170 EndZ=0
    g2: LineSegment StartX=170 StartY=170 StartZ=0 EndX=0 EndY=170 EndZ=0
    g3: LineSegment StartX=0 StartY=170 StartZ=0 EndX=0 EndY=0 EndZ=0
    g4: Circle CenterX=6.35 CenterY=4.8997 CenterZ=0 NormalX=0 NormalY=0 NormalZ=1 AngleXU=0 Radius=2
    g5: Circle CenterX=163.65 CenterY=4.8997 CenterZ=0 NormalX=0 NormalY=0 NormalZ=1 AngleXU=0 Radius=2
    g6: Circle CenterX=6.35 CenterY=159.84 CenterZ=0 NormalX=0 NormalY=0 NormalZ=1 AngleXU=0 Radius=2
    g7: Circle CenterX=163.65 CenterY=136.98 CenterZ=0 NormalX=0 NormalY=0 NormalZ=1 AngleXU=0 Radius=2
    g8: LineSegment [constr] StartX=6.35 StartY=159.84 StartZ=0 EndX=6.35 EndY=4.8997 EndZ=0
    g9: LineSegment [constr] StartX=6.35 StartY=4.8997 StartZ=0 EndX=163.65 EndY=4.8997 EndZ=0
    g10: LineSegment [constr] StartX=163.65 StartY=4.8997 StartZ=0 EndX=163.65 EndY=136.98 EndZ=0
    g11: LineSegment [constr] StartX=163.65 StartY=136.98 StartZ=0 EndX=6.35 EndY=136.98 EndZ=0
  constraints (32):
    c: Coincident(g0,g1)
    c: Coincident(g1,g2)
    c: Coincident(g2,g3)
    c: Coincident(g3,g0)
    c: Horizontal(g0)
    c: Horizontal(g2)
    c: Vertical(g1)
    c: Vertical(g3)
    c: Coincident(g0,g-1)
    c: DistanceX(g2,g2) = 170
    c: DistanceY(g1,g1) = 170
    c: Diameter(g4) = 4
    c: Diameter(g5) = 4
    c: Diameter(g6) = 4
    c: Diameter(g7) = 4
    c: Coincident(g8,g6)
    c: Coincident(g8,g4)
    c: Vertical(g8)
    c: Coincident(g9,g4)
    c: Coincident(g9,g5)
    c: Horizontal(g9)
    c: Coincident(g10,g5)
    c: Coincident(g10,g7)
    c: Vertical(g10)
    c: Distance(g6,g2) = 10.16
    c: Distance(g6,g3) = 6.35
    c: Distance(g7,g1) = 6.35
    c: DistanceY(g5) = 4.8997
    c: Coincident(g11,g7)
    c: PointOnObject(g11,g8)
    c: Horizontal(g11)
    c: Distance(g6,g11) = 22.86
FEATURE [PartDesign::Pad] Pad004
  Direction = (0,0,1)
  Length = 1.6
  Length2 = 10
  Profile = -> Sketch004
  ReferenceAxis = -> Sketch004 [N_Axis]
  Refine = true
  Suppressed = false
  Type = 0
FEATURE [Sketcher::SketchObject] Sketch010
  ArcFitTolerance = 1e-06
  AttachmentSupport = -> [XY_Plane005]
  FullyConstrained = false
  MakeInternals = false
  MapMode = 5
  sketch-geometry (11):
    g0: LineSegment [constr] StartX=0 StartY=0 StartZ=0 EndX=170 EndY=0 EndZ=0
    g1: LineSegment [constr] StartX=170 StartY=0 StartZ=0 EndX=170 EndY=170 EndZ=0
    g2: LineSegment [constr] StartX=170 StartY=170 StartZ=0 EndX=0 EndY=170 EndZ=0
    g3: LineSegment [constr] StartX=0 StartY=170 StartZ=0 EndX=0 EndY=0 EndZ=0
    g4: LineSegment StartX=12 StartY=174 StartZ=0 EndX=12 EndY=138 EndZ=0
    g5: LineSegment StartX=175 StartY=174 StartZ=0 EndX=12 EndY=174 EndZ=0
    g6: LineSegment [constr] StartX=175 StartY=138 StartZ=0 EndX=175 EndY=151.25 EndZ=0
    g7: LineSegment StartX=175 StartY=151.25 StartZ=0 EndX=175 EndY=174 EndZ=0
    g8: LineSegment StartX=12 StartY=138 StartZ=0 EndX=151.759 EndY=138 EndZ=0
    g9: LineSegment [constr] StartX=151.759 StartY=138 StartZ=0 EndX=175 EndY=138 EndZ=0
    g10: LineSegment StartX=151.759 StartY=138 StartZ=0 EndX=175 EndY=151.25 EndZ=0
  constraints (29):
    c: Coincident(g0,g1)
    c: Coincident(g1,g2)
    c: Coincident(g2,g3)
    c: Coincident(g3,g0)
    c: Horizontal(g0)
    c: Horizontal(g2)
    c: Vertical(g1)
    c: Vertical(g3)
    c: Distance(g1,g3) = 170
    c: Distance(g0,g2) = 170
    c: Coincident(g0,g-1)
    c: Coincident(g4,g8)
    c: Coincident(g9,g6)
    c: Coincident(g7,g5)
    c: Coincident(g5,g4)
    c: Vertical(g4)
    c: Horizontal(g5)
    c: DistanceX(g4) = 12
    c: Distance(g4,g2) = 4
    c: Distance(g7,g1) = 5
    c: DistanceY(g6,g7) = 36
    c: Coincident(g6,g7)
    c: Vertical(g6)
    c: Vertical(g7)
    c: Coincident(g8,g9)
    c: Horizontal(g8)
    c: Horizontal(g9)
    c: Coincident(g10,g8)
    c: Coincident(g10,g6)
FEATURE [PartDesign::Pad] Pad007
  BaseFeature = -> Pad004
  Direction = (0,0,1)
  Length = 45
  Length2 = 10
  Profile = -> Sketch010
  ReferenceAxis = -> Sketch010 [N_Axis]
  Refine = true
  Suppressed = false
  Type = 0
FEATURE [Sketcher::SketchObject] Sketch042
  ArcFitTolerance = 1e-06
  AttachmentSupport = -> [XY_Plane005]
  FullyConstrained = true
  MakeInternals = false
  MapMode = 5
  sketch-geometry (8):
    g0: LineSegment [constr] StartX=0 StartY=0 StartZ=0 EndX=170 EndY=0 EndZ=0
    g1: LineSegment [constr] StartX=170 StartY=0 StartZ=0 EndX=170 EndY=170 EndZ=0
    g2: LineSegment [constr] StartX=170 StartY=170 StartZ=0 EndX=0 EndY=170 EndZ=0
    g3: LineSegment [constr] StartX=0 StartY=170 StartZ=0 EndX=0 EndY=0 EndZ=0
    g4: LineSegment StartX=43 StartY=122 StartZ=0 EndX=43 EndY=42 EndZ=0
    g5: LineSegment StartX=43 StartY=42 StartZ=0 EndX=153 EndY=42 EndZ=0
    g6: LineSegment StartX=153 StartY=42 StartZ=0 EndX=153 EndY=122 EndZ=0
    g7: LineSegment StartX=153 StartY=122 StartZ=0 EndX=43 EndY=122 EndZ=0
  constraints (23):
    c: Coincident(g0,g1)
    c: Coincident(g1,g2)
    c: Coincident(g2,g3)
    c: Coincident(g3,g0)
    c: Horizontal(g0)
    c: Horizontal(g2)
    c: Vertical(g1)
    c: Vertical(g3)
    c: Distance(g1,g3) = 170
    c: Distance(g0,g2) = 170
    c: Coincident(g0,g-1)
    c: Coincident(g4,g5)
    c: Coincident(g5,g6)
    c: Coincident(g6,g7)
    c: Coincident(g7,g4)
    c: Vertical(g4)
    c: Vertical(g6)
    c: Horizontal(g5)
    c: Horizontal(g7)
    c: Distance(g4,g6) = 110
    c: Distance(g5,g7) = 80
    c: Distance(g5,g1) = 17
    c: DistanceY(g5) = 42
FEATURE [PartDesign::Pad] Pad022
  BaseFeature = -> Pad007
  Direction = (0,0,1)
  Length = 36
  Length2 = 10
  Profile = -> Sketch042
  ReferenceAxis = -> Sketch042 [N_Axis]
  Refine = true
  Suppressed = false
  Type = 0
FEATURE [PartDesign::Pad] Pad029
  BaseFeature = -> Pad022
  Direction = (0,0,1)
  Length = 5
  Length2 = 10
  Profile = -> Sketch010
  ReferenceAxis = -> Sketch010 [N_Axis]
  Refine = true
  Reversed = true
  Suppressed = false
  Type = 0
FEATURE [PartDesign::Body] Body002
  AllowCompound = false
  Group = -> [Sketch004,Pad004,Sketch010,Pad007,Sketch042,Pad022,Pad029]
  Origin = -> Origin005
  Placement = pos=(59,-86,-131) rot=(0,0,1;0rad)
  Tip = -> Pad029
COMPONENT P10 — recipe-attached ("PSU001", modeled in this document).
Construction recipe (the document's own serialized feature program — sketch geometry with constraints, then the solid features built on it; lengths are millimeters unless a unit is written):

FEATURE [Sketcher::SketchObject] Sketch
  ArcFitTolerance = 1e-06
  AttachmentSupport = -> [XY_Plane001]
  FullyConstrained = true
  MakeInternals = false
  MapMode = 5
  expr: Constraints[10] = <<components>>.psu_h
  expr: Constraints[30] = <<components>>.m3_hole
  expr: Constraints[9] = <<components>>.psu_w
  sketch-geometry (13):
    g0: LineSegment StartX=0 StartY=0 StartZ=0 EndX=55 EndY=0 EndZ=0
    g1: LineSegment StartX=55 StartY=0 StartZ=0 EndX=55 EndY=170 EndZ=0
    g2: LineSegment StartX=55 StartY=170 StartZ=0 EndX=0 EndY=170 EndZ=0
    g3: LineSegment StartX=0 StartY=170 StartZ=0 EndX=0 EndY=0 EndZ=0
    g4: LineSegment [constr] StartX=10.85 StartY=13 StartZ=0 EndX=44.15 EndY=13 EndZ=0
    g5: LineSegment [constr] StartX=44.15 StartY=13 StartZ=0 EndX=44.15 EndY=157 EndZ=0
    g6: LineSegment [constr] StartX=44.15 StartY=157 StartZ=0 EndX=10.85 EndY=157 EndZ=0
    g7: LineSegment [constr] StartX=10.85 StartY=157 StartZ=0 EndX=10.85 EndY=13 EndZ=0
    g8: GeomPoint [constr] X=27.5 Y=85 Z=0
    g9: Circle CenterX=10.85 CenterY=157 CenterZ=0 NormalX=0 NormalY=0 NormalZ=1 AngleXU=0 Radius=1.75
    g10: Circle CenterX=44.15 CenterY=157 CenterZ=0 NormalX=0 NormalY=0 NormalZ=1 AngleXU=0 Radius=1.75
    g11: Circle CenterX=10.85 CenterY=13 CenterZ=0 NormalX=0 NormalY=0 NormalZ=1 AngleXU=0 Radius=1.75
    g12: Circle CenterX=44.15 CenterY=13 CenterZ=0 NormalX=0 NormalY=0 NormalZ=1 AngleXU=0 Radius=1.75
  constraints (31):
    c: Coincident(g0,g1)
    c: Coincident(g1,g2)
    c: Coincident(g2,g3)
    c: Coincident(g3,g0)
    c: Horizontal(g0)
    c: Horizontal(g2)
    c: Vertical(g1)
    c: Vertical(g3)
    c: Coincident(g0,g-1)
    c: DistanceX(g2,g2) = 55
    c: DistanceY(g1,g1) = 170
    c: Coincident(g4,g5)
    c: Coincident(g5,g6)
    c: Coincident(g6,g7)
    c: Coincident(g7,g4)
    c: Horizontal(g4)
    c: Horizontal(g6)
    c: Vertical(g5)
    c: Vertical(g7)
    c: Symmetric(g6,g4,g8)
    c: Distance(g5,g7) = 33.3
    c: Distance(g4,g6) = 144
    c: Symmetric(g2,g0,g8)
    c: Coincident(g9,g6)
    c: Coincident(g10,g5)
    c: Coincident(g11,g4)
    c: Coincident(g12,g4)
    c: Equal(g9,g10)
    c: Equal(g10,g11)
    c: Equal(g11,g12)
    c: Diameter(g11) = 3.5
FEATURE [PartDesign::Pad] Pad
  Direction = (0,0,1)
  Length = 25
  Length2 = 10
  Profile = -> Sketch
  ReferenceAxis = -> Sketch [N_Axis]
  Refine = true
  Suppressed = false
  Type = 0
  expr: Length = <<components>>.psu_d
FEATURE [PartDesign::Plane] DatumPlane
  AttachmentSupport = -> [Pad]
  Length = 92.6491
  MapMode = 5
  Placement = pos=(0,170,0) rot=(0,0.707107,0.707107;3.14159rad)
  ResizeMode = 0
  Width = 62.6491
FEATURE [Sketcher::SketchObject] Sketch001
  ArcFitTolerance = 1e-06
  AttachmentSupport = -> [DatumPlane]
  FullyConstrained = true
  MakeInternals = false
  MapMode = 5
  Placement = pos=(0,170,0) rot=(0,0.707107,0.707107;3.14159rad)
  expr: Constraints[10] = <<components>>.psu_d
  expr: Constraints[9] = <<components>>.psu_w
  sketch-geometry (5):
    g0: LineSegment [constr] StartX=-55 StartY=25 StartZ=0 EndX=-55 EndY=0 EndZ=0
    g1: LineSegment [constr] StartX=-55 StartY=0 StartZ=0 EndX=0 EndY=0 EndZ=0
    g2: LineSegment [constr] StartX=0 StartY=0 StartZ=0 EndX=0 EndY=25 EndZ=0
    g3: LineSegment [constr] StartX=0 StartY=25 StartZ=0 EndX=-55 EndY=25 EndZ=0
    g4: Circle CenterX=-27.5 CenterY=12.5 CenterZ=0 NormalX=0 NormalY=0 NormalZ=1 AngleXU=0 Radius=5
  constraints (13):
    c: Coincident(g0,g1)
    c: Coincident(g1,g2)
    c: Coincident(g2,g3)
    c: Coincident(g3,g0)
    c: Vertical(g0)
    c: Vertical(g2)
    c: Horizontal(g1)
    c: Horizontal(g3)
    c: Coincident(g1,g-1)
    c: DistanceX(g3,g3) = 55
    c: DistanceY(g0,g0) = 25
    c: Diameter(g4) = 10
    c: Symmetric(g0,g1,g4)
FEATURE [PartDesign::Pad] Pad001
  BaseFeature = -> Pad
  Direction = (0,1,-2e-16)
  Length = 7
  Length2 = 10
  Profile = -> Sketch001
  ReferenceAxis = -> Sketch001 [N_Axis]
  Refine = true
  Suppressed = false
  Type = 0
FEATURE [PartDesign::Body] Body
  AllowCompound = false
  Group = -> [Sketch,Pad,DatumPlane,Sketch001,Pad001]
  Origin = -> Origin001
  Tip = -> Pad001
COMPONENT P11 — recipe-attached ("SCREEN001", modeled in this document).
Construction recipe (the document's own serialized feature program — sketch geometry with constraints, then the solid features built on it; lengths are millimeters unless a unit is written):

FEATURE [Sketcher::SketchObject] Sketch002
  ArcFitTolerance = 1e-06
  AttachmentSupport = -> [XY_Plane003]
  FullyConstrained = true
  MakeInternals = false
  MapMode = 5
  expr: Constraints[26] = <<components>>.screen_glass_corner_radius
  expr: Constraints[5] = <<components>>.screen_w
  expr: Constraints[6] = <<components>>.screen_h
  sketch-geometry (12):
    g0: LineSegment StartX=1 StartY=4.954e-13 StartZ=0 EndX=366.9 EndY=4.954e-13 EndZ=0
    g1: LineSegment StartX=367.9 StartY=1 StartZ=0 EndX=367.9 EndY=221.4 EndZ=0
    g2: LineSegment StartX=366.9 StartY=222.4 StartZ=0 EndX=1 EndY=222.4 EndZ=0
    g3: LineSegment StartX=4.954e-13 StartY=221.4 StartZ=0 EndX=4.954e-13 EndY=1 EndZ=0
    g4: ArcOfCircle CenterX=1 CenterY=1 CenterZ=0 NormalX=0 NormalY=0 NormalZ=1 AngleXU=0 Radius=1 StartAngle=3.14159 EndAngle=4.71239
    g5: GeomPoint [constr] X=0 Y=0 Z=0
    g6: ArcOfCircle CenterX=1 CenterY=221.4 CenterZ=0 NormalX=0 NormalY=0 NormalZ=1 AngleXU=0 Radius=1 StartAngle=1.5708 EndAngle=3.14159
    g7: GeomPoint [constr] X=0 Y=222.4 Z=0
    g8: ArcOfCircle CenterX=366.9 CenterY=221.4 CenterZ=0 NormalX=0 NormalY=0 NormalZ=1 AngleXU=0 Radius=1 StartAngle=-3.1388e-12 EndAngle=1.5708
    g9: GeomPoint [constr] X=367.9 Y=222.4 Z=0
    g10: ArcOfCircle CenterX=366.9 CenterY=1 CenterZ=0 NormalX=0 NormalY=0 NormalZ=1 AngleXU=0 Radius=1 StartAngle=4.71239 EndAngle=6.28319
    g11: GeomPoint [constr] X=367.9 Y=0 Z=0
  constraints (27):
    c: Horizontal(g0)
    c: Horizontal(g2)
    c: Vertical(g1)
    c: Vertical(g3)
    c: Coincident(g5,g-1)
    c: DistanceX(g5,g11) = 367.9
    c: DistanceY(g5,g7) = 222.4
    c: PointOnObject(g5,g0)
    c: PointOnObject(g5,g3)
    c: Tangent(g0,g4) = -1.5708
    c: Tangent(g3,g4) = -1.5708
    c: PointOnObject(g7,g3)
    c: PointOnObject(g7,g2)
    c: Tangent(g3,g6) = -1.5708
    c: Tangent(g2,g6) = -1.5708
    c: PointOnObject(g9,g2)
    c: PointOnObject(g9,g1)
    c: Tangent(g2,g8) = -1.5708
    c: Tangent(g1,g8) = -1.5708
    c: PointOnObject(g11,g0)
    c: PointOnObject(g11,g1)
    c: Tangent(g0,g10) = -1.5708
    c: Tangent(g1,g10) = -1.5708
    c: Equal(g4,g6)
    c: Equal(g6,g8)
    c: Equal(g8,g10)
    c: Radius(g4) = 1
FEATURE [PartDesign::Pad] Pad002
  Direction = (0,0,1)
  Length = 1.5
  Length2 = 10
  Profile = -> Sketch002
  ReferenceAxis = -> Sketch002 [N_Axis]
  Refine = true
  Reversed = true
  Suppressed = false
  Type = 0
  expr: Length = <<components>>.screen_glass_d
FEATURE [Sketcher::SketchObject] Sketch003
  ArcFitTolerance = 1e-06
  AttachmentSupport = -> [XY_Plane003]
  FullyConstrained = true
  MakeInternals = false
  MapMode = 5
  expr: Constraints[22] = <<components>>.screen_h - 4
  expr: Constraints[23] = <<components>>.screen_w - 2.5
  sketch-geometry (8):
    g0: LineSegment StartX=6.5 StartY=12.5 StartZ=0 EndX=6.5 EndY=218.4 EndZ=0
    g1: LineSegment StartX=6.5 StartY=218.4 StartZ=0 EndX=365.4 EndY=218.4 EndZ=0
    g2: LineSegment StartX=365.4 StartY=218.4 StartZ=0 EndX=365.4 EndY=12.5 EndZ=0
    g3: LineSegment StartX=365.4 StartY=12.5 StartZ=0 EndX=330.4 EndY=12.5 EndZ=0
    g4: LineSegment StartX=330.4 StartY=12.5 StartZ=0 EndX=330.4 EndY=1 EndZ=0
    g5: LineSegment StartX=330.4 StartY=1 StartZ=0 EndX=41.5 EndY=1 EndZ=0
    g6: LineSegment StartX=41.5 StartY=1 StartZ=0 EndX=41.5 EndY=12.5 EndZ=0
    g7: LineSegment StartX=41.5 StartY=12.5 StartZ=0 EndX=6.5 EndY=12.5 EndZ=0
  constraints (24):
    c: Vertical(g0)
    c: Coincident(g0,g1)
    c: Horizontal(g1)
    c: Coincident(g1,g2)
    c: Vertical(g2)
    c: Coincident(g2,g3)
    c: Horizontal(g3)
    c: Coincident(g3,g4)
    c: Vertical(g4)
    c: Coincident(g4,g5)
    c: Coincident(g5,g6)
    c: Vertical(g6)
    c: Coincident(g6,g7)
    c: Coincident(g7,g0)
    c: Horizontal(g7)
    c: Horizontal(g5)
    c: Equal(g7,g3)
    c: DistanceX(g3,g3) = 35
    c: DistanceY(g2) = 12.5
    c: DistanceY(g4) = 1
    c: Equal(g6,g4)
    c: DistanceX(g0) = 6.5
    c: DistanceY(g0) = 218.4
    c: DistanceX(g1) = 365.4
FEATURE [PartDesign::Pad] Pad003
  BaseFeature = -> Pad002
  Direction = (0,0,1)
  Length = 6.5
  Length2 = 10
  Profile = -> Sketch003
  ReferenceAxis = -> Sketch003 [N_Axis]
  Refine = true
  Reversed = true
  Suppressed = false
  Type = 0
  expr: Length = <<components>>.screen_panel_d
FEATURE [Sketcher::SketchObject] Sketch005
  ArcFitTolerance = 1e-06
  AttachmentSupport = -> [XY_Plane003]
  FullyConstrained = true
  MakeInternals = false
  MapMode = 5
  sketch-geometry (4):
    g0: LineSegment StartX=17 StartY=43 StartZ=0 EndX=217 EndY=43 EndZ=0
    g1: LineSegment StartX=217 StartY=43 StartZ=0 EndX=217 EndY=93 EndZ=0
    g2: LineSegment StartX=217 StartY=93 StartZ=0 EndX=17 EndY=93 EndZ=0
    g3: LineSegment StartX=17 StartY=93 StartZ=0 EndX=17 EndY=43 EndZ=0
  constraints (12):
    c: Coincident(g0,g1)
    c: Coincident(g1,g2)
    c: Coincident(g2,g3)
    c: Coincident(g3,g0)
    c: Horizontal(g0)
    c: Horizontal(g2)
    c: Vertical(g1)
    c: Vertical(g3)
    c: Distance(g1,g3) = 200
    c: Distance(g0,g2) = 50
    c: DistanceX(g0) = 17
    c: DistanceY(g0) = 43
FEATURE [PartDesign::Pad] Pad005
  BaseFeature = -> Pad003
  Direction = (0,0,1)
  Length = 19
  Length2 = 10
  Profile = -> Sketch005
  ReferenceAxis = -> Sketch005 [N_Axis]
  Refine = true
  Reversed = true
  Suppressed = false
  Type = 0
  expr: Length = <<components>>.screen_pcb_d
FEATURE [PartDesign::Body] Body001
  AllowCompound = false
  Group = -> [Sketch002,Pad002,Sketch003,Pad003,Sketch005,Pad005]
  Origin = -> Origin003
  Tip = -> Pad005
COMPONENT P12 — recipe-attached ("top back cover001", modeled in this document).
Construction recipe (the document's own serialized feature program — sketch geometry with constraints, then the solid features built on it; lengths are millimeters unless a unit is written):

FEATURE [Sketcher::SketchObject] Sketch085
  ArcFitTolerance = 1e-06
  AttachmentSupport = -> [XY_Plane041]
  FullyConstrained = false
  MakeInternals = false
  MapMode = 5
  expr: Constraints[18] = <<components>>.m3_hole
  expr: Constraints[9] = <<components>>.frame_w - 2 * 65
  sketch-geometry (10):
    g0: LineSegment StartX=65 StartY=-236.705 StartZ=0 EndX=65 EndY=-250.705 EndZ=0
    g1: LineSegment StartX=65 StartY=-250.705 StartZ=0 EndX=310 EndY=-250.705 EndZ=0
    g2: LineSegment StartX=310 StartY=-250.705 StartZ=0 EndX=310 EndY=-236.705 EndZ=0
    g3: LineSegment StartX=310 StartY=-236.705 StartZ=0 EndX=65 EndY=-236.705 EndZ=0
    g4: LineSegment [constr] StartX=65 StartY=-243.705 StartZ=0 EndX=310 EndY=-243.705 EndZ=0
    g5: GeomPoint X=187.5 Y=-243.705 Z=0
    g6: Circle CenterX=162.5 CenterY=-243.705 CenterZ=0 NormalX=0 NormalY=0 NormalZ=1 AngleXU=0 Radius=1.75
    g7: Circle CenterX=90 CenterY=-243.705 CenterZ=0 NormalX=0 NormalY=0 NormalZ=1 AngleXU=0 Radius=1.75
    g8: Circle CenterX=212.5 CenterY=-243.705 CenterZ=0 NormalX=0 NormalY=0 NormalZ=1 AngleXU=0 Radius=1.75
    g9: Circle CenterX=285 CenterY=-243.705 CenterZ=0 NormalX=0 NormalY=0 NormalZ=1 AngleXU=0 Radius=1.75
  constraints (25):
    c: Coincident(g0,g1)
    c: Coincident(g1,g2)
    c: Coincident(g2,g3)
    c: Coincident(g3,g0)
    c: Vertical(g0)
    c: Vertical(g2)
    c: Horizontal(g1)
    c: Horizontal(g3)
    c: DistanceX(g0) = 65
    c: DistanceX(g3,g3) = 245
    c: PointOnObject(g4,g0)
    c: Horizontal(g4)
    c: Symmetric(g4,g4,g5)
    c: PointOnObject(g6,g4)
    c: PointOnObject(g7,g4)
    c: Equal(g7,g6)
    c: Equal(g6,g8)
    c: Equal(g8,g9)
    c: Diameter(g7) = 3.5
    c: DistanceY(g2,g2) = 14
    c: Symmetric(g2,g2,g4)
    c: DistanceX(g7) = 90
    c: Symmetric(g7,g9,g5)
    c: Symmetric(g8,g6,g5)
    c: Distance(g6,g8) = 50
FEATURE [PartDesign::Pad] Pad043
  Direction = (0,0,1)
  Length = 7
  Length2 = 10
  Profile = -> Sketch085
  ReferenceAxis = -> Sketch085 [N_Axis]
  Refine = true
  Suppressed = false
  Type = 0
FEATURE [PartDesign::Chamfer] Chamfer010
  Angle = 45
  Base = -> Pad043 [Edge23,Edge14,Edge17,Edge20]
  BaseFeature = -> Pad043
  ChamferType = 0
  FlipDirection = false
  Refine = true
  Size = 2
  Size2 = 1
  SupportTransform = false
  Suppressed = false
  UseAllEdges = false
FEATURE [Sketcher::SketchObject] Sketch086
  ArcFitTolerance = 1e-06
  AttachmentSupport = -> [XY_Plane041]
  FullyConstrained = false
  MakeInternals = false
  MapMode = 5
  sketch-geometry (4):
    g0: LineSegment StartX=309.981 StartY=-253.638 StartZ=0 EndX=309.981 EndY=-250.638 EndZ=0
    g1: LineSegment StartX=309.981 StartY=-250.638 StartZ=0 EndX=154.072 EndY=-250.638 EndZ=0
    g2: LineSegment StartX=154.072 StartY=-250.638 StartZ=0 EndX=154.072 EndY=-253.638 EndZ=0
    g3: LineSegment StartX=154.072 StartY=-253.638 StartZ=0 EndX=309.981 EndY=-253.638 EndZ=0
  constraints (9):
    c: Coincident(g0,g1)
    c: Coincident(g1,g2)
    c: Coincident(g2,g3)
    c: Coincident(g3,g0)
    c: Vertical(g0)
    c: Vertical(g2)
    c: Horizontal(g1)
    c: Horizontal(g3)
    c: DistanceY(g2,g2) = 3
FEATURE [PartDesign::Pad] Pad044
  BaseFeature = -> Chamfer010
  Direction = (0,0,1)
  Length = 7
  Length2 = 10
  Profile = -> Sketch086
  ReferenceAxis = -> Sketch086 [N_Axis]
  Refine = true
  Suppressed = false
  Type = 0
FEATURE [PartDesign::Plane] DatumPlane023
  AttachmentOffset = pos=(0,0,7) rot=(0,0,1;0rad)
  AttachmentSupport = -> [XY_Plane041]
  Length = 396.104
  MapMode = 5
  Placement = pos=(0,0,7) rot=(0,0,1;0rad)
  ResizeMode = 0
  Width = 339.742
FEATURE [Sketcher::SketchObject] Sketch097
  ArcFitTolerance = 1e-06
  AttachmentSupport = -> [DatumPlane023]
  FullyConstrained = false
  MakeInternals = false
  MapMode = 5
  Placement = pos=(0,0,7) rot=(0,0,1;0rad)
  sketch-geometry (4):
    g0: LineSegment StartX=105.345 StartY=-233.638 StartZ=0 EndX=105.345 EndY=-255.638 EndZ=0
    g1: LineSegment StartX=105.345 StartY=-255.638 StartZ=0 EndX=113.345 EndY=-255.638 EndZ=0
    g2: LineSegment StartX=113.345 StartY=-255.638 StartZ=0 EndX=113.345 EndY=-233.638 EndZ=0
    g3: LineSegment StartX=113.345 StartY=-233.638 StartZ=0 EndX=105.345 EndY=-233.638 EndZ=0
  constraints (10):
    c: Coincident(g0,g1)
    c: Coincident(g1,g2)
    c: Coincident(g2,g3)
    c: Coincident(g3,g0)
    c: Vertical(g0)
    c: Vertical(g2)
    c: Horizontal(g1)
    c: Horizontal(g3)
    c: Distance(g0,g2) = 8
    c: Distance(g1,g3) = 22
FEATURE [PartDesign::Pocket] Pocket043
  BaseFeature = -> Pad044
  Direction = (0,0,-1)
  Length = 4
  Length2 = 5
  Profile = -> Sketch097
  ReferenceAxis = -> Sketch097 [N_Axis]
  Refine = true
  Suppressed = false
  Type = 0
FEATURE [PartDesign::Fillet] Fillet003
  Base = -> Pocket043 [Edge27,Edge26]
  BaseFeature = -> Pocket043
  Radius = 3.99
  Refine = true
  SupportTransform = false
  Suppressed = false
  UseAllEdges = false
FEATURE [PartDesign::Body] Body019
  AllowCompound = false
  Group = -> [Sketch085,Pad043,Chamfer010,Sketch086,Pad044,Sketch097,DatumPlane023,Pocket043,Fillet003]
  Origin = -> Origin041
  Tip = -> Fillet003
PROVENANCE & LICENSES
A FreeCAD (.FCStd) document from a public repository crawl; recipes are the document's own serialized feature recipes (and, for linked parts, companion documents' recipes).
License: as declared in the source repository (recorded in the dataset sidecar).
